FCSTD DOCUMENT  (FreeCAD 1.0R39285 (Git))
Label: CNC-MILL-1
License: All rights reserved
LicenseURL: http://en.wikipedia.org/wiki/All_rights_reserved
objects: Part::Feature×28, Sketcher::SketchObject×24, PartDesign::Pad×18, PartDesign::Body×17, App::Part×15, Part::FeaturePython×14, PartDesign::Pocket×6, PartDesign::Hole×1, PartDesign::Chamfer×1, App::FeaturePython×1
note: 185 computed .brp shape members not serialized (recipe doc carries the construction recipe); baked Part::Feature solids carry a one-line shape summary decoded from their .brp

FEATURE [Part::Feature] Part__Feature  label="NEMA23 - PSM57HS2A54-2P"
  Placement = pos=(161.359,-628.852,-80) rot=(0,0,1;0rad)
  shape: bbox 56.89 x 76.8 x 56.89 mm, 146 faces, 2 solids (baked)
FEATURE [Part::Feature] Part__Feature001  label="NEMA23 - PSM57HS2A54-2P001"
  Placement = pos=(161.359,-628.852,0) rot=(0,0,1;0rad)
  shape: bbox 56.89 x 76.8 x 56.89 mm, 146 faces, 2 solids (baked)
FEATURE [Part::Feature] Part__Feature002  label="NEMA23 - PSM57HS2A54-2P002"
  Placement = pos=(379,33,35) rot=(0,0,1;3.14159rad)
  shape: bbox 56.89 x 76.8 x 56.89 mm, 146 faces, 2 solids (baked)
FEATURE [Sketcher::SketchObject] Sketch
  ArcFitTolerance = 1e-06
  AttachmentSupport = -> [XY_Plane002]
  FullyConstrained = true
  MakeInternals = false
  MapMode = 5
  sketch-geometry (4):
    g0: LineSegment StartX=0 StartY=0 StartZ=0 EndX=257 EndY=0 EndZ=0
    g1: LineSegment StartX=257 StartY=0 StartZ=0 EndX=257 EndY=264 EndZ=0
    g2: LineSegment StartX=257 StartY=264 StartZ=0 EndX=0 EndY=264 EndZ=0
    g3: LineSegment StartX=0 StartY=264 StartZ=0 EndX=0 EndY=0 EndZ=0
  constraints (11):
    c: Coincident(g0,g1)
    c: Coincident(g1,g2)
    c: Coincident(g2,g3)
    c: Coincident(g3,g0)
    c: Horizontal(g0)
    c: Horizontal(g2)
    c: Vertical(g1)
    c: Vertical(g3)
    c: Distance(g1,g3) = 257
    c: Distance(g0,g2) = 264
    c: Coincident(g0,g-1)
FEATURE [PartDesign::Pad] Pad
  Direction = (0,0,1)
  Length = 10
  Length2 = 10
  Profile = -> Sketch
  ReferenceAxis = -> Sketch [N_Axis]
  Suppressed = false
  Type = 0
FEATURE [PartDesign::Body] Body
  AllowCompound = false
  Group = -> [Sketch,Pad]
  Origin = -> Origin002
  Placement = pos=(0,0,-51) rot=(0,0,1;0rad)
  Tip = -> Pad
FEATURE [App::Part] Part001  label="stone table"
  Group = -> [Body]
  Origin = -> Origin
  Placement = pos=(59,-361,0) rot=(0,0,1;0rad)
FEATURE [Sketcher::SketchObject] Sketch001
  ArcFitTolerance = 1e-06
  AttachmentSupport = -> [XZ_Plane004]
  FullyConstrained = true
  MakeInternals = false
  MapMode = 5
  Placement = pos=(0,0,0) rot=(1,0,0;1.5708rad)
  sketch-geometry (14):
    g0: LineSegment StartX=0 StartY=-2 StartZ=0 EndX=0 EndY=-38 EndZ=0
    g1: LineSegment StartX=2 StartY=-40 StartZ=0 EndX=38 EndY=-40 EndZ=0
    g2: LineSegment StartX=40 StartY=-38 StartZ=0 EndX=40 EndY=-2 EndZ=0
    g3: LineSegment StartX=38 StartY=0 StartZ=0 EndX=2 EndY=0 EndZ=0
    g4: ArcOfCircle CenterX=2 CenterY=-2 CenterZ=0 NormalX=0 NormalY=0 NormalZ=1 AngleXU=0 Radius=2 StartAngle=1.5708 EndAngle=3.14159
    g5: ArcOfCircle CenterX=2 CenterY=-38 CenterZ=0 NormalX=0 NormalY=0 NormalZ=1 AngleXU=0 Radius=2 StartAngle=3.14159 EndAngle=4.71239
    g6: ArcOfCircle CenterX=38 CenterY=-38 CenterZ=0 NormalX=0 NormalY=0 NormalZ=1 AngleXU=0 Radius=2 StartAngle=4.71239 EndAngle=6.28319
    g7: ArcOfCircle CenterX=38 CenterY=-2 CenterZ=0 NormalX=0 NormalY=0 NormalZ=1 AngleXU=0 Radius=2 StartAngle=0 EndAngle=1.5708
    g8: LineSegment StartX=2 StartY=-2 StartZ=0 EndX=2 EndY=-38 EndZ=0
    g9: LineSegment StartX=2 StartY=-38 StartZ=0 EndX=38 EndY=-38 EndZ=0
    g10: LineSegment StartX=38 StartY=-38 StartZ=0 EndX=38 EndY=-2 EndZ=0
    g11: LineSegment StartX=38 StartY=-2 StartZ=0 EndX=2 EndY=-2 EndZ=0
    g12: GeomPoint [constr] X=0 Y=0 Z=0
    g13: GeomPoint [constr] X=40 Y=-40 Z=0
  constraints (31):
    c: Tangent(g0,g4) = -1.5708
    c: Tangent(g0,g5) = -1.5708
    c: Tangent(g1,g5) = -1.5708
    c: Tangent(g1,g6) = -1.5708
    c: Tangent(g2,g6) = -1.5708
    c: Tangent(g2,g7) = -1.5708
    c: Tangent(g3,g7) = -1.5708
    c: Tangent(g3,g4) = -1.5708
    c: Vertical(g0)
    c: Vertical(g2)
    c: Horizontal(g1)
    c: Horizontal(g3)
    c: Equal(g4,g5)
    c: Equal(g5,g6)
    c: Equal(g6,g7)
    c: Coincident(g8,g9)
    c: Coincident(g9,g10)
    c: Coincident(g10,g11)
    c: Coincident(g11,g8)
    c: Coincident(g8,g4)
    c: Coincident(g9,g5)
    c: Coincident(g10,g6)
    c: Coincident(g11,g7)
    c: PointOnObject(g12,g0)
    c: PointOnObject(g12,g3)
    c: PointOnObject(g13,g1)
    c: PointOnObject(g13,g2)
    c: Distance(g0,g2) = 40
    c: Distance(g1,g3) = 40
    c: Radius(g5) = 2
    c: Coincident(g12,g-1)
FEATURE [PartDesign::Pad] Pad001
  Direction = (0,-1,2e-16)
  Length = 400
  Length2 = 10
  Placement = pos=(0,0,0) rot=(1,0,0;1.5708rad)
  Profile = -> Sketch001
  ReferenceAxis = -> Sketch001 [N_Axis]
  Suppressed = false
  Type = 0
FEATURE [PartDesign::Body] Body001
  AllowCompound = false
  Group = -> [Sketch001,Pad001]
  Origin = -> Origin004
  Placement = pos=(-54,0,0) rot=(0,0,1;0rad)
  Tip = -> Pad001
FEATURE [Sketcher::SketchObject] Sketch002
  ArcFitTolerance = 1e-06
  AttachmentSupport = -> [XZ_Plane005]
  FullyConstrained = true
  MakeInternals = false
  MapMode = 5
  Placement = pos=(0,0,0) rot=(1,0,0;1.5708rad)
  sketch-geometry (14):
    g0: LineSegment StartX=0 StartY=-2 StartZ=0 EndX=0 EndY=-38 EndZ=0
    g1: LineSegment StartX=2 StartY=-40 StartZ=0 EndX=38 EndY=-40 EndZ=0
    g2: LineSegment StartX=40 StartY=-38 StartZ=0 EndX=40 EndY=-2 EndZ=0
    g3: LineSegment StartX=38 StartY=0 StartZ=0 EndX=2 EndY=0 EndZ=0
    g4: ArcOfCircle CenterX=2 CenterY=-2 CenterZ=0 NormalX=0 NormalY=0 NormalZ=1 AngleXU=0 Radius=2 StartAngle=1.5708 EndAngle=3.14159
    g5: ArcOfCircle CenterX=2 CenterY=-38 CenterZ=0 NormalX=0 NormalY=0 NormalZ=1 AngleXU=0 Radius=2 StartAngle=3.14159 EndAngle=4.71239
    g6: ArcOfCircle CenterX=38 CenterY=-38 CenterZ=0 NormalX=0 NormalY=0 NormalZ=1 AngleXU=0 Radius=2 StartAngle=4.71239 EndAngle=6.28319
    g7: ArcOfCircle CenterX=38 CenterY=-2 CenterZ=0 NormalX=0 NormalY=0 NormalZ=1 AngleXU=0 Radius=2 StartAngle=0 EndAngle=1.5708
    g8: LineSegment StartX=2 StartY=-2 StartZ=0 EndX=2 EndY=-38 EndZ=0
    g9: LineSegment StartX=2 StartY=-38 StartZ=0 EndX=38 EndY=-38 EndZ=0
    g10: LineSegment StartX=38 StartY=-38 StartZ=0 EndX=38 EndY=-2 EndZ=0
    g11: LineSegment StartX=38 StartY=-2 StartZ=0 EndX=2 EndY=-2 EndZ=0
    g12: GeomPoint [constr] X=0 Y=0 Z=0
    g13: GeomPoint [constr] X=40 Y=-40 Z=0
  constraints (31):
    c: Tangent(g0,g4) = -1.5708
    c: Tangent(g0,g5) = -1.5708
    c: Tangent(g1,g5) = -1.5708
    c: Tangent(g1,g6) = -1.5708
    c: Tangent(g2,g6) = -1.5708
    c: Tangent(g2,g7) = -1.5708
    c: Tangent(g3,g7) = -1.5708
    c: Tangent(g3,g4) = -1.5708
    c: Vertical(g0)
    c: Vertical(g2)
    c: Horizontal(g1)
    c: Horizontal(g3)
    c: Equal(g4,g5)
    c: Equal(g5,g6)
    c: Equal(g6,g7)
    c: Coincident(g8,g9)
    c: Coincident(g9,g10)
    c: Coincident(g10,g11)
    c: Coincident(g11,g8)
    c: Coincident(g8,g4)
    c: Coincident(g9,g5)
    c: Coincident(g10,g6)
    c: Coincident(g11,g7)
    c: PointOnObject(g12,g0)
    c: PointOnObject(g12,g3)
    c: PointOnObject(g13,g1)
    c: PointOnObject(g13,g2)
    c: Distance(g0,g2) = 40
    c: Distance(g1,g3) = 40
    c: Radius(g5) = 2
    c: Coincident(g12,g-1)
FEATURE [PartDesign::Pad] Pad002
  Direction = (0,-1,2e-16)
  Length = 400
  Length2 = 10
  Placement = pos=(0,0,0) rot=(1,0,0;1.5708rad)
  Profile = -> Sketch002
  ReferenceAxis = -> Sketch002 [N_Axis]
  Suppressed = false
  Type = 0
FEATURE [PartDesign::Body] Body002
  AllowCompound = false
  Group = -> [Sketch002,Pad002]
  Origin = -> Origin005
  Placement = pos=(346,0,0) rot=(0,0,1;0rad)
  Tip = -> Pad002
FEATURE [Sketcher::SketchObject] Sketch004
  ArcFitTolerance = 1e-06
  AttachmentSupport = -> [XZ_Plane007]
  FullyConstrained = true
  MakeInternals = false
  MapMode = 5
  Placement = pos=(0,0,0) rot=(1,0,0;1.5708rad)
  sketch-geometry (14):
    g0: LineSegment StartX=0 StartY=-2 StartZ=0 EndX=0 EndY=-38 EndZ=0
    g1: LineSegment StartX=2 StartY=-40 StartZ=0 EndX=38 EndY=-40 EndZ=0
    g2: LineSegment StartX=40 StartY=-38 StartZ=0 EndX=40 EndY=-2 EndZ=0
    g3: LineSegment StartX=38 StartY=0 StartZ=0 EndX=2 EndY=0 EndZ=0
    g4: ArcOfCircle CenterX=2 CenterY=-2 CenterZ=0 NormalX=0 NormalY=0 NormalZ=1 AngleXU=0 Radius=2 StartAngle=1.5708 EndAngle=3.14159
    g5: ArcOfCircle CenterX=2 CenterY=-38 CenterZ=0 NormalX=0 NormalY=0 NormalZ=1 AngleXU=0 Radius=2 StartAngle=3.14159 EndAngle=4.71239
    g6: ArcOfCircle CenterX=38 CenterY=-38 CenterZ=0 NormalX=0 NormalY=0 NormalZ=1 AngleXU=0 Radius=2 StartAngle=4.71239 EndAngle=6.28319
    g7: ArcOfCircle CenterX=38 CenterY=-2 CenterZ=0 NormalX=0 NormalY=0 NormalZ=1 AngleXU=0 Radius=2 StartAngle=0 EndAngle=1.5708
    g8: LineSegment StartX=2 StartY=-2 StartZ=0 EndX=2 EndY=-38 EndZ=0
    g9: LineSegment StartX=2 StartY=-38 StartZ=0 EndX=38 EndY=-38 EndZ=0
    g10: LineSegment StartX=38 StartY=-38 StartZ=0 EndX=38 EndY=-2 EndZ=0
    g11: LineSegment StartX=38 StartY=-2 StartZ=0 EndX=2 EndY=-2 EndZ=0
    g12: GeomPoint [constr] X=0 Y=0 Z=0
    g13: GeomPoint [constr] X=40 Y=-40 Z=0
  constraints (31):
    c: Tangent(g0,g4) = -1.5708
    c: Tangent(g0,g5) = -1.5708
    c: Tangent(g1,g5) = -1.5708
    c: Tangent(g1,g6) = -1.5708
    c: Tangent(g2,g6) = -1.5708
    c: Tangent(g2,g7) = -1.5708
    c: Tangent(g3,g7) = -1.5708
    c: Tangent(g3,g4) = -1.5708
    c: Vertical(g0)
    c: Vertical(g2)
    c: Horizontal(g1)
    c: Horizontal(g3)
    c: Equal(g4,g5)
    c: Equal(g5,g6)
    c: Equal(g6,g7)
    c: Coincident(g8,g9)
    c: Coincident(g9,g10)
    c: Coincident(g10,g11)
    c: Coincident(g11,g8)
    c: Coincident(g8,g4)
    c: Coincident(g9,g5)
    c: Coincident(g10,g6)
    c: Coincident(g11,g7)
    c: PointOnObject(g12,g0)
    c: PointOnObject(g12,g3)
    c: PointOnObject(g13,g1)
    c: PointOnObject(g13,g2)
    c: Distance(g0,g2) = 40
    c: Distance(g1,g3) = 40
    c: Radius(g5) = 2
    c: Coincident(g12,g-1)
FEATURE [PartDesign::Pad] Pad004
  Direction = (0,-1,2e-16)
  Length = 400
  Length2 = 10
  Placement = pos=(0,0,0) rot=(1,0,0;1.5708rad)
  Profile = -> Sketch004
  ReferenceAxis = -> Sketch004 [N_Axis]
  Suppressed = false
  Type = 0
FEATURE [Sketcher::SketchObject] Sketch005
  ArcFitTolerance = 1e-06
  AttachmentSupport = -> [XY_Plane009]
  FullyConstrained = true
  MakeInternals = false
  MapMode = 5
  sketch-geometry (16):
    g0: LineSegment StartX=0 StartY=68 StartZ=0 EndX=65 EndY=68 EndZ=0
    g1: LineSegment StartX=65 StartY=68 StartZ=0 EndX=65 EndY=6.00001 EndZ=0
    g2: LineSegment StartX=65 StartY=6.00001 StartZ=0 EndX=59 EndY=0 EndZ=0
    g3: LineSegment StartX=0 StartY=68 StartZ=0 EndX=0 EndY=6.00001 EndZ=0
    g4: LineSegment StartX=0 StartY=6.00001 StartZ=0 EndX=6 EndY=0 EndZ=0
    g5: LineSegment StartX=6 StartY=0 StartZ=0 EndX=59 EndY=0 EndZ=0
    g6: ArcOfCircle CenterX=52.5 CenterY=10 CenterZ=0 NormalX=0 NormalY=0 NormalZ=1 AngleXU=0 Radius=2 StartAngle=3.14159 EndAngle=6.28319
    g7: ArcOfCircle CenterX=52.5 CenterY=52 CenterZ=0 NormalX=0 NormalY=0 NormalZ=1 AngleXU=0 Radius=2 StartAngle=0 EndAngle=3.14159
    g8: LineSegment StartX=50.5 StartY=10 StartZ=0 EndX=50.5 EndY=52 EndZ=0
    g9: LineSegment StartX=54.5 StartY=10 StartZ=0 EndX=54.5 EndY=52 EndZ=0
    g10: ArcOfCircle CenterX=12.5 CenterY=10 CenterZ=0 NormalX=0 NormalY=0 NormalZ=1 AngleXU=0 Radius=2 StartAngle=3.14159 EndAngle=6.28319
    g11: ArcOfCircle CenterX=12.5 CenterY=52 CenterZ=0 NormalX=0 NormalY=0 NormalZ=1 AngleXU=0 Radius=2 StartAngle=0 EndAngle=3.14159
    g12: LineSegment StartX=14.5 StartY=10 StartZ=0 EndX=14.5 EndY=52 EndZ=0
    g13: LineSegment StartX=10.5 StartY=10 StartZ=0 EndX=10.5 EndY=52 EndZ=0
    g14: LineSegment [constr] StartX=32.5 StartY=68 StartZ=0 EndX=32.5 EndY=0 EndZ=0
    g15: LineSegment [constr] StartX=65 StartY=31 StartZ=0 EndX=0 EndY=31 EndZ=0
  constraints (46):
    c: PointOnObject(g0,g-2)
    c: Distance(g0) = 65
    c: Horizontal(g0)
    c: Distance(g1) = 62
    c: Coincident(g1,g0)
    c: Vertical(g1)
    c: Angle(g-1,g2) = -2.35619
    c: Coincident(g2,g1)
    c: PointOnObject(g2,g-1)
    c: Distance(g3) = 62
    c: Vertical(g3)
    c: Coincident(g4,g3)
    c: Coincident(g5,g4)
    c: Coincident(g5,g2)
    c: Horizontal(g5)
    c: Tangent(g6,g8) = 1.5708
    c: Tangent(g6,g9) = -1.5708
    c: Tangent(g7,g8) = 1.5708
    c: Tangent(g7,g9) = -1.5708
    c: Equal(g6,g7)
    c: Vertical(g9)
    c: Distance(g6,g7) = 42
    c: Radius(g6) = 2
    c: Tangent(g10,g12) = -1.5708
    c: Tangent(g10,g13) = 1.5708
    c: Tangent(g11,g12) = -1.5708
    c: Tangent(g11,g13) = 1.5708
    c: Equal(g10,g11)
    c: Vertical(g13)
    c: Distance(g10,g11) = 42
    c: Radius(g10) = 2
    c: Distance(g-1,g4) = 6
    c: DistanceX(g4,g2) = 53
    c: DistanceX(g10,g6) = 40
    c: Symmetric(g0,g0,g14)
    c: Vertical(g14)
    c: DistanceX(g10,g14) = 20
    c: DistanceX(g3,g1) = 65
    c: PointOnObject(g15,g1)
    c: PointOnObject(g15,g3)
    c: Horizontal(g15)
    c: DistanceY(g-1,g15) = 31
    c: DistanceY(g10,g15) = 21
    c: Horizontal(g10,g6)
    c: Horizontal(g3,g1)
    c: Horizontal(g4,g14)
FEATURE [PartDesign::Pad] Pad005
  Direction = (0,0,1)
  Length = 3
  Length2 = 10
  Profile = -> Sketch005
  ReferenceAxis = -> Sketch005 [N_Axis]
  Suppressed = false
  Type = 0
FEATURE [Part::Feature] Part__Feature003  label="MGN9-H"
  shape: bbox 20 x 8 x 29.9 mm, 47 faces (baked)
FEATURE [Part::Feature] Part__Feature004  label="MGN9-H001"
  shape: bbox 20 x 7.7 x 4.1 mm, 23 faces (baked)
FEATURE [Part::Feature] Part__Feature005  label="MGN9-H002"
  shape: bbox 2.603 x 2.603 x 1.283 mm, 15 faces (baked)
FEATURE [Part::Feature] Part__Feature006  label="MGN9-H003"
  shape: bbox 2.603 x 2.603 x 1.283 mm, 15 faces (baked)
FEATURE [Part::Feature] Part__Feature007  label="MGN9-H004"
  shape: bbox 20 x 7.7 x 0.9 mm, 57 faces (baked)
FEATURE [Part::Feature] Part__Feature008  label="MGN9-H005"
  shape: bbox 20 x 7.7 x 4.1 mm, 23 faces (baked)
FEATURE [Part::Feature] Part__Feature009  label="MGN9-H006"
  shape: bbox 20 x 7.7 x 0.9 mm, 57 faces (baked)
FEATURE [Part::Feature] Part__Feature010  label="MGN9-H007"
  shape: bbox 2.603 x 2.603 x 1.283 mm, 15 faces (baked)
FEATURE [Part::Feature] Part__Feature011  label="MGN9-H008"
  shape: bbox 2.603 x 2.603 x 1.283 mm, 15 faces (baked)
FEATURE [App::Part] MGN9_H  label="MGN9-H009 block"
  Group = -> [Part__Feature003,Part__Feature004,Part__Feature005,Part__Feature006,Part__Feature007,Part__Feature008,Part__Feature009,Part__Feature010,Part__Feature011]
  Origin = -> Origin010
  Placement = pos=(19,-161.179,6) rot=(0,0.707107,0.707107;3.14159rad)
FEATURE [Part::Feature] Part__Feature012  label="MGN9"
  Placement = pos=(-3.25,-34,143.25) rot=(0,0,1;1.5708rad)
  shape: bbox 6.5 x 9 x 250 mm, 130 faces (baked)
FEATURE [App::Part] Part004  label="MGN9 rail"
  Group = -> [Part__Feature012]
  Origin = -> Origin011
  Placement = pos=(53,8.58707,0) rot=(-0.58,-0.58,0.58;4.18879rad)
FEATURE [Sketcher::SketchObject] Sketch006
  ArcFitTolerance = 1e-06
  AttachmentSupport = -> [Pad005]
  FullyConstrained = true
  MakeInternals = false
  MapMode = 5
  Placement = pos=(0,0,3) rot=(0,0,1;0rad)
  sketch-geometry (4):
    g0: LineSegment StartX=0 StartY=68 StartZ=0 EndX=0 EndY=65 EndZ=0
    g1: LineSegment StartX=0 StartY=65 StartZ=0 EndX=65 EndY=65 EndZ=0
    g2: LineSegment StartX=65 StartY=65 StartZ=0 EndX=65 EndY=68 EndZ=0
    g3: LineSegment StartX=65 StartY=68 StartZ=0 EndX=0 EndY=68 EndZ=0
  constraints (12):
    c: Coincident(g0,g1)
    c: Coincident(g1,g2)
    c: Coincident(g2,g3)
    c: Coincident(g3,g0)
    c: Vertical(g0)
    c: Vertical(g2)
    c: Horizontal(g1)
    c: Horizontal(g3)
    c: Distance(g0,g2) = 65
    c: Distance(g1,g3) = 3
    c: PointOnObject(g0,g-2)
    c: DistanceY(g-1,g0) = 68
FEATURE [PartDesign::Pad] Pad006
  BaseFeature = -> Pad005
  Direction = (0,0,1)
  Length = 65
  Length2 = 10
  Profile = -> Sketch006
  ReferenceAxis = -> Sketch006 [N_Axis]
  Suppressed = false
  Type = 0
FEATURE [Sketcher::SketchObject] Sketch007
  ArcFitTolerance = 1e-06
  AttachmentSupport = -> [Pad006]
  ExternalGeometry = -> [Pad006]
  FullyConstrained = false
  MakeInternals = false
  MapMode = 5
  Placement = pos=(0,65,0) rot=(1,0,0;1.5708rad)
  sketch-geometry (15):
    g0: LineSegment StartX=0 StartY=68 StartZ=0 EndX=6 EndY=68 EndZ=0
    g1: LineSegment StartX=0 StartY=68 StartZ=0 EndX=0 EndY=62 EndZ=0
    g2: LineSegment StartX=6 StartY=68 StartZ=0 EndX=0 EndY=62 EndZ=0
    g3: LineSegment [constr] StartX=32.5 StartY=68 StartZ=0 EndX=32.5 EndY=3 EndZ=0
    g4: Circle CenterX=9 CenterY=59 CenterZ=0 NormalX=0 NormalY=0 NormalZ=1 AngleXU=0 Radius=2.6
    g5: LineSegment [constr] StartX=0 StartY=35.5 StartZ=0 EndX=65 EndY=35.5 EndZ=0
    g6: Circle CenterX=32.5 CenterY=35.5 CenterZ=0 NormalX=0 NormalY=0 NormalZ=1 AngleXU=0 Radius=19.1
    g7: LineSegment StartX=65 StartY=68 StartZ=0 EndX=59 EndY=68 EndZ=0
    g8: LineSegment StartX=65 StartY=68 StartZ=0 EndX=65 EndY=62 EndZ=0
    g9: LineSegment StartX=59 StartY=68 StartZ=0 EndX=65 EndY=62 EndZ=0
    g10: Circle CenterX=56 CenterY=12 CenterZ=0 NormalX=0 NormalY=0 NormalZ=1 AngleXU=0 Radius=2.6
    g11: Circle CenterX=56 CenterY=59 CenterZ=0 NormalX=0 NormalY=0 NormalZ=1 AngleXU=0 Radius=2.6
    g12: Circle CenterX=56 CenterY=12 CenterZ=0 NormalX=0 NormalY=0 NormalZ=1 AngleXU=0 Radius=2.6
    g13: Circle CenterX=9 CenterY=12 CenterZ=0 NormalX=0 NormalY=0 NormalZ=1 AngleXU=0 Radius=2.6
    g14: Circle CenterX=9 CenterY=12 CenterZ=0 NormalX=0 NormalY=0 NormalZ=1 AngleXU=0 Radius=2.6
  constraints (32):
    c: Distance(g0) = 6
    c: PointOnObject(g0,g-2)
    c: Horizontal(g0)
    c: Distance(g1) = 6
    c: Coincident(g1,g0)
    c: PointOnObject(g1,g-2)
    c: Coincident(g2,g0)
    c: Coincident(g2,g1)
    c: Vertical(g3)
    c: DistanceX(g4,g3) = 23.5
    c: Distance(g5) = 65
    c: Symmetric(g-3,g-3,g5)
    c: Horizontal(g5)
    c: Diameter(g6) = 38.2
    c: Symmetric(g5,g5,g6)
    c: DistanceY(g-3,g0) = 65
    c: Distance(g7) = 6
    c: Horizontal(g7)
    c: Distance(g8) = 6
    c: Coincident(g8,g7)
    c: Coincident(g9,g7)
    c: Coincident(g9,g8)
    c: Diameter(g12) = 5.2
    c: Coincident(g12,g10)
    c: Horizontal(g3,g0)
    c: Symmetric(g4,g11,g3)
    c: Diameter(g14) = 5.2
    c: Coincident(g14,g13)
    c: Symmetric(g13,g10,g3)
    c: Horizontal(g3,g-3)
    c: Vertical(g5,g8)
    c: DistanceX(g0,g3) = 32.5
FEATURE [PartDesign::Pocket] Pocket
  BaseFeature = -> Pad006
  Direction = (0,1,-2e-16)
  Length = 3
  Length2 = 5
  Profile = -> Sketch007
  ReferenceAxis = -> Sketch007 [N_Axis]
  Suppressed = false
  Type = 0
FEATURE [PartDesign::Body] Body005
  AllowCompound = false
  Group = -> [Sketch005,Pad005,Sketch006,Pad006,Sketch007,Pocket]
  Origin = -> Origin009
  Placement = pos=(12,0,0) rot=(0,0,1;0rad)
  Tip = -> Pocket
FEATURE [App::Part] Part003  label="bracket nema 23"
  Group = -> [Body005]
  Origin = -> Origin008
  Placement = pos=(63,70,0) rot=(0,0,1;3.14159rad)
FEATURE [App::Part] Part005  label="TR8x2 screw"
  Origin = -> Origin012
FEATURE [Part::FeaturePython] ThreadedRod  label="8x400-ThreadedRod"  # WARN: FeaturePython — macro-defined, semantics opaque (R4)
  Diameter = 29
  DiameterCustom = 8
  Invert = false
  LeftHanded = false
  Length = 400
  MatchOuter = false
  OffsetAngle = 0
  PitchCustom = 2
  Placement = pos=(19,-418,35) rot=(1,0,0;1.5708rad)
  Thread = false
  Type = 4
FEATURE [Part::Feature] Part__Feature013  label="Coupler 6.35-8mm Without Screw"
  shape: bbox 20.93 x 20.57 x 29.69 mm, 170 faces (baked)
FEATURE [Part::Feature] Part__Feature014  label="80 x 60 x 32 - EG 86-32 HG (All closed) [similar]"
  Placement = pos=(169,-174.833,-46.8462) rot=(-1,0,0;4.71239rad)
  shape: bbox 800 x 600 x 320 mm, 837 faces (baked)
FEATURE [Part::Feature] Part__Feature015  label="60 x 40 x 27 - EG 64-27 HG (All closed) [similar]"
  Placement = pos=(186,-256,-359) rot=(-0.57735,0.57735,0.57735;4.18879rad)
  shape: bbox 398 x 598 x 270 mm, 709 faces (baked)
FEATURE [App::Part] Part006  label="Bottom container"
  Group = -> [Part__Feature014,Part__Feature015]
  Origin = -> Origin015
FEATURE [Sketcher::SketchObject] Sketch008
  ArcFitTolerance = 1e-06
  AttachmentSupport = -> [XZ_Plane017]
  FullyConstrained = true
  MakeInternals = false
  MapMode = 5
  Placement = pos=(0,0,0) rot=(1,0,0;1.5708rad)
  sketch-geometry (14):
    g0: LineSegment StartX=0 StartY=-2 StartZ=0 EndX=0 EndY=-38 EndZ=0
    g1: LineSegment StartX=2 StartY=-40 StartZ=0 EndX=38 EndY=-40 EndZ=0
    g2: LineSegment StartX=40 StartY=-38 StartZ=0 EndX=40 EndY=-2 EndZ=0
    g3: LineSegment StartX=38 StartY=0 StartZ=0 EndX=2 EndY=0 EndZ=0
    g4: ArcOfCircle CenterX=2 CenterY=-2 CenterZ=0 NormalX=0 NormalY=0 NormalZ=1 AngleXU=0 Radius=2 StartAngle=1.5708 EndAngle=3.14159
    g5: ArcOfCircle CenterX=2 CenterY=-38 CenterZ=0 NormalX=0 NormalY=0 NormalZ=1 AngleXU=0 Radius=2 StartAngle=3.14159 EndAngle=4.71239
    g6: ArcOfCircle CenterX=38 CenterY=-38 CenterZ=0 NormalX=0 NormalY=0 NormalZ=1 AngleXU=0 Radius=2 StartAngle=4.71239 EndAngle=6.28319
    g7: ArcOfCircle CenterX=38 CenterY=-2 CenterZ=0 NormalX=0 NormalY=0 NormalZ=1 AngleXU=0 Radius=2 StartAngle=0 EndAngle=1.5708
    g8: LineSegment StartX=2 StartY=-2 StartZ=0 EndX=2 EndY=-38 EndZ=0
    g9: LineSegment StartX=2 StartY=-38 StartZ=0 EndX=38 EndY=-38 EndZ=0
    g10: LineSegment StartX=38 StartY=-38 StartZ=0 EndX=38 EndY=-2 EndZ=0
    g11: LineSegment StartX=38 StartY=-2 StartZ=0 EndX=2 EndY=-2 EndZ=0
    g12: GeomPoint [constr] X=0 Y=0 Z=0
    g13: GeomPoint [constr] X=40 Y=-40 Z=0
  constraints (31):
    c: Tangent(g0,g4) = -1.5708
    c: Tangent(g0,g5) = -1.5708
    c: Tangent(g1,g5) = -1.5708
    c: Tangent(g1,g6) = -1.5708
    c: Tangent(g2,g6) = -1.5708
    c: Tangent(g2,g7) = -1.5708
    c: Tangent(g3,g7) = -1.5708
    c: Tangent(g3,g4) = -1.5708
    c: Vertical(g0)
    c: Vertical(g2)
    c: Horizontal(g1)
    c: Horizontal(g3)
    c: Equal(g4,g5)
    c: Equal(g5,g6)
    c: Equal(g6,g7)
    c: Coincident(g8,g9)
    c: Coincident(g9,g10)
    c: Coincident(g10,g11)
    c: Coincident(g11,g8)
    c: Coincident(g8,g4)
    c: Coincident(g9,g5)
    c: Coincident(g10,g6)
    c: Coincident(g11,g7)
    c: PointOnObject(g12,g0)
    c: PointOnObject(g12,g3)
    c: PointOnObject(g13,g1)
    c: PointOnObject(g13,g2)
    c: Distance(g0,g2) = 40
    c: Distance(g1,g3) = 40
    c: Radius(g5) = 2
    c: Coincident(g12,g-1)
FEATURE [PartDesign::Pad] Pad007
  Direction = (0,-1,2e-16)
  Length = 400
  Length2 = 10
  Placement = pos=(0,0,0) rot=(1,0,0;1.5708rad)
  Profile = -> Sketch008
  ReferenceAxis = -> Sketch008 [N_Axis]
  Suppressed = false
  Type = 0
FEATURE [PartDesign::Body] Body006
  AllowCompound = false
  Group = -> [Sketch008,Pad007]
  Origin = -> Origin017
  Placement = pos=(386,40,0) rot=(-0.57735,0.57735,0.57735;4.18879rad)
  Tip = -> Pad007
FEATURE [Sketcher::SketchObject] Sketch009
  ArcFitTolerance = 1e-06
  AttachmentSupport = -> [XZ_Plane018]
  FullyConstrained = true
  MakeInternals = false
  MapMode = 5
  Placement = pos=(0,0,0) rot=(1,0,0;1.5708rad)
  sketch-geometry (14):
    g0: LineSegment StartX=0 StartY=-2 StartZ=0 EndX=0 EndY=-38 EndZ=0
    g1: LineSegment StartX=2 StartY=-40 StartZ=0 EndX=38 EndY=-40 EndZ=0
    g2: LineSegment StartX=40 StartY=-38 StartZ=0 EndX=40 EndY=-2 EndZ=0
    g3: LineSegment StartX=38 StartY=0 StartZ=0 EndX=2 EndY=0 EndZ=0
    g4: ArcOfCircle CenterX=2 CenterY=-2 CenterZ=0 NormalX=0 NormalY=0 NormalZ=1 AngleXU=0 Radius=2 StartAngle=1.5708 EndAngle=3.14159
    g5: ArcOfCircle CenterX=2 CenterY=-38 CenterZ=0 NormalX=0 NormalY=0 NormalZ=1 AngleXU=0 Radius=2 StartAngle=3.14159 EndAngle=4.71239
    g6: ArcOfCircle CenterX=38 CenterY=-38 CenterZ=0 NormalX=0 NormalY=0 NormalZ=1 AngleXU=0 Radius=2 StartAngle=4.71239 EndAngle=6.28319
    g7: ArcOfCircle CenterX=38 CenterY=-2 CenterZ=0 NormalX=0 NormalY=0 NormalZ=1 AngleXU=0 Radius=2 StartAngle=0 EndAngle=1.5708
    g8: LineSegment StartX=2 StartY=-2 StartZ=0 EndX=2 EndY=-38 EndZ=0
    g9: LineSegment StartX=2 StartY=-38 StartZ=0 EndX=38 EndY=-38 EndZ=0
    g10: LineSegment StartX=38 StartY=-38 StartZ=0 EndX=38 EndY=-2 EndZ=0
    g11: LineSegment StartX=38 StartY=-2 StartZ=0 EndX=2 EndY=-2 EndZ=0
    g12: GeomPoint [constr] X=0 Y=0 Z=0
    g13: GeomPoint [constr] X=40 Y=-40 Z=0
  constraints (31):
    c: Tangent(g0,g4) = -1.5708
    c: Tangent(g0,g5) = -1.5708
    c: Tangent(g1,g5) = -1.5708
    c: Tangent(g1,g6) = -1.5708
    c: Tangent(g2,g6) = -1.5708
    c: Tangent(g2,g7) = -1.5708
    c: Tangent(g3,g7) = -1.5708
    c: Tangent(g3,g4) = -1.5708
    c: Vertical(g0)
    c: Vertical(g2)
    c: Horizontal(g1)
    c: Horizontal(g3)
    c: Equal(g4,g5)
    c: Equal(g5,g6)
    c: Equal(g6,g7)
    c: Coincident(g8,g9)
    c: Coincident(g9,g10)
    c: Coincident(g10,g11)
    c: Coincident(g11,g8)
    c: Coincident(g8,g4)
    c: Coincident(g9,g5)
    c: Coincident(g10,g6)
    c: Coincident(g11,g7)
    c: PointOnObject(g12,g0)
    c: PointOnObject(g12,g3)
    c: PointOnObject(g13,g1)
    c: PointOnObject(g13,g2)
    c: Distance(g0,g2) = 40
    c: Distance(g1,g3) = 40
    c: Radius(g5) = 2
    c: Coincident(g12,g-1)
FEATURE [PartDesign::Pad] Pad008
  Direction = (0,-1,2e-16)
  Length = 400
  Length2 = 10
  Placement = pos=(0,0,0) rot=(1,0,0;1.5708rad)
  Profile = -> Sketch009
  ReferenceAxis = -> Sketch009 [N_Axis]
  Suppressed = false
  Type = 0
FEATURE [PartDesign::Body] Body007
  AllowCompound = false
  Group = -> [Sketch009,Pad008]
  Origin = -> Origin018
  Placement = pos=(-54,40,9.77e-14) rot=(-0.57735,0.57735,0.57735;4.18879rad)
  Tip = -> Pad008
FEATURE [Sketcher::SketchObject] Sketch010
  ArcFitTolerance = 1e-06
  AttachmentSupport = -> [XZ_Plane019]
  FullyConstrained = true
  MakeInternals = false
  MapMode = 5
  Placement = pos=(0,0,0) rot=(1,0,0;1.5708rad)
  sketch-geometry (14):
    g0: LineSegment StartX=0 StartY=-2 StartZ=0 EndX=0 EndY=-38 EndZ=0
    g1: LineSegment StartX=2 StartY=-40 StartZ=0 EndX=38 EndY=-40 EndZ=0
    g2: LineSegment StartX=40 StartY=-38 StartZ=0 EndX=40 EndY=-2 EndZ=0
    g3: LineSegment StartX=38 StartY=0 StartZ=0 EndX=2 EndY=0 EndZ=0
    g4: ArcOfCircle CenterX=2 CenterY=-2 CenterZ=0 NormalX=0 NormalY=0 NormalZ=1 AngleXU=0 Radius=2 StartAngle=1.5708 EndAngle=3.14159
    g5: ArcOfCircle CenterX=2 CenterY=-38 CenterZ=0 NormalX=0 NormalY=0 NormalZ=1 AngleXU=0 Radius=2 StartAngle=3.14159 EndAngle=4.71239
    g6: ArcOfCircle CenterX=38 CenterY=-38 CenterZ=0 NormalX=0 NormalY=0 NormalZ=1 AngleXU=0 Radius=2 StartAngle=4.71239 EndAngle=6.28319
    g7: ArcOfCircle CenterX=38 CenterY=-2 CenterZ=0 NormalX=0 NormalY=0 NormalZ=1 AngleXU=0 Radius=2 StartAngle=0 EndAngle=1.5708
    g8: LineSegment StartX=2 StartY=-2 StartZ=0 EndX=2 EndY=-38 EndZ=0
    g9: LineSegment StartX=2 StartY=-38 StartZ=0 EndX=38 EndY=-38 EndZ=0
    g10: LineSegment StartX=38 StartY=-38 StartZ=0 EndX=38 EndY=-2 EndZ=0
    g11: LineSegment StartX=38 StartY=-2 StartZ=0 EndX=2 EndY=-2 EndZ=0
    g12: GeomPoint [constr] X=0 Y=0 Z=0
    g13: GeomPoint [constr] X=40 Y=-40 Z=0
  constraints (31):
    c: Tangent(g0,g4) = -1.5708
    c: Tangent(g0,g5) = -1.5708
    c: Tangent(g1,g5) = -1.5708
    c: Tangent(g1,g6) = -1.5708
    c: Tangent(g2,g6) = -1.5708
    c: Tangent(g2,g7) = -1.5708
    c: Tangent(g3,g7) = -1.5708
    c: Tangent(g3,g4) = -1.5708
    c: Vertical(g0)
    c: Vertical(g2)
    c: Horizontal(g1)
    c: Horizontal(g3)
    c: Equal(g4,g5)
    c: Equal(g5,g6)
    c: Equal(g6,g7)
    c: Coincident(g8,g9)
    c: Coincident(g9,g10)
    c: Coincident(g10,g11)
    c: Coincident(g11,g8)
    c: Coincident(g8,g4)
    c: Coincident(g9,g5)
    c: Coincident(g10,g6)
    c: Coincident(g11,g7)
    c: PointOnObject(g12,g0)
    c: PointOnObject(g12,g3)
    c: PointOnObject(g13,g1)
    c: PointOnObject(g13,g2)
    c: Distance(g0,g2) = 40
    c: Distance(g1,g3) = 40
    c: Radius(g5) = 2
    c: Coincident(g12,g-1)
FEATURE [PartDesign::Pad] Pad009
  Direction = (0,-1,2e-16)
  Length = 400
  Length2 = 10
  Placement = pos=(0,0,0) rot=(1,0,0;1.5708rad)
  Profile = -> Sketch010
  ReferenceAxis = -> Sketch010 [N_Axis]
  Suppressed = false
  Type = 0
FEATURE [PartDesign::Body] Body008
  AllowCompound = false
  Group = -> [Sketch010,Pad009]
  Origin = -> Origin019
  Placement = pos=(386,-400,9.77e-14) rot=(-0.57735,0.57735,0.57735;4.18879rad)
  Tip = -> Pad009
FEATURE [Sketcher::SketchObject] Sketch011
  ArcFitTolerance = 1e-06
  AttachmentSupport = -> [XZ_Plane020]
  FullyConstrained = true
  MakeInternals = false
  MapMode = 5
  Placement = pos=(0,0,0) rot=(1,0,0;1.5708rad)
  sketch-geometry (14):
    g0: LineSegment StartX=0 StartY=-2 StartZ=0 EndX=0 EndY=-38 EndZ=0
    g1: LineSegment StartX=2 StartY=-40 StartZ=0 EndX=38 EndY=-40 EndZ=0
    g2: LineSegment StartX=40 StartY=-38 StartZ=0 EndX=40 EndY=-2 EndZ=0
    g3: LineSegment StartX=38 StartY=0 StartZ=0 EndX=2 EndY=0 EndZ=0
    g4: ArcOfCircle CenterX=2 CenterY=-2 CenterZ=0 NormalX=0 NormalY=0 NormalZ=1 AngleXU=0 Radius=2 StartAngle=1.5708 EndAngle=3.14159
    g5: ArcOfCircle CenterX=2 CenterY=-38 CenterZ=0 NormalX=0 NormalY=0 NormalZ=1 AngleXU=0 Radius=2 StartAngle=3.14159 EndAngle=4.71239
    g6: ArcOfCircle CenterX=38 CenterY=-38 CenterZ=0 NormalX=0 NormalY=0 NormalZ=1 AngleXU=0 Radius=2 StartAngle=4.71239 EndAngle=6.28319
    g7: ArcOfCircle CenterX=38 CenterY=-2 CenterZ=0 NormalX=0 NormalY=0 NormalZ=1 AngleXU=0 Radius=2 StartAngle=0 EndAngle=1.5708
    g8: LineSegment StartX=2 StartY=-2 StartZ=0 EndX=2 EndY=-38 EndZ=0
    g9: LineSegment StartX=2 StartY=-38 StartZ=0 EndX=38 EndY=-38 EndZ=0
    g10: LineSegment StartX=38 StartY=-38 StartZ=0 EndX=38 EndY=-2 EndZ=0
    g11: LineSegment StartX=38 StartY=-2 StartZ=0 EndX=2 EndY=-2 EndZ=0
    g12: GeomPoint [constr] X=0 Y=0 Z=0
    g13: GeomPoint [constr] X=40 Y=-40 Z=0
  constraints (31):
    c: Tangent(g0,g4) = -1.5708
    c: Tangent(g0,g5) = -1.5708
    c: Tangent(g1,g5) = -1.5708
    c: Tangent(g1,g6) = -1.5708
    c: Tangent(g2,g6) = -1.5708
    c: Tangent(g2,g7) = -1.5708
    c: Tangent(g3,g7) = -1.5708
    c: Tangent(g3,g4) = -1.5708
    c: Vertical(g0)
    c: Vertical(g2)
    c: Horizontal(g1)
    c: Horizontal(g3)
    c: Equal(g4,g5)
    c: Equal(g5,g6)
    c: Equal(g6,g7)
    c: Coincident(g8,g9)
    c: Coincident(g9,g10)
    c: Coincident(g10,g11)
    c: Coincident(g11,g8)
    c: Coincident(g8,g4)
    c: Coincident(g9,g5)
    c: Coincident(g10,g6)
    c: Coincident(g11,g7)
    c: PointOnObject(g12,g0)
    c: PointOnObject(g12,g3)
    c: PointOnObject(g13,g1)
    c: PointOnObject(g13,g2)
    c: Distance(g0,g2) = 40
    c: Distance(g1,g3) = 40
    c: Radius(g5) = 2
    c: Coincident(g12,g-1)
FEATURE [PartDesign::Pad] Pad010
  Direction = (0,-1,2e-16)
  Length = 400
  Length2 = 10
  Placement = pos=(0,0,0) rot=(1,0,0;1.5708rad)
  Profile = -> Sketch011
  ReferenceAxis = -> Sketch011 [N_Axis]
  Suppressed = false
  Type = 0
FEATURE [PartDesign::Body] Body009
  AllowCompound = false
  Group = -> [Sketch011,Pad010]
  Origin = -> Origin020
  Placement = pos=(-54,-400,1.954e-13) rot=(-0.57735,0.57735,0.57735;4.18879rad)
  Tip = -> Pad010
FEATURE [Sketcher::SketchObject] Sketch012
  ArcFitTolerance = 1e-06
  AttachmentSupport = -> [XZ_Plane021]
  FullyConstrained = true
  MakeInternals = false
  MapMode = 5
  Placement = pos=(0,0,0) rot=(1,0,0;1.5708rad)
  sketch-geometry (14):
    g0: LineSegment StartX=0 StartY=-2 StartZ=0 EndX=0 EndY=-38 EndZ=0
    g1: LineSegment StartX=2 StartY=-40 StartZ=0 EndX=38 EndY=-40 EndZ=0
    g2: LineSegment StartX=40 StartY=-38 StartZ=0 EndX=40 EndY=-2 EndZ=0
    g3: LineSegment StartX=38 StartY=0 StartZ=0 EndX=2 EndY=0 EndZ=0
    g4: ArcOfCircle CenterX=2 CenterY=-2 CenterZ=0 NormalX=0 NormalY=0 NormalZ=1 AngleXU=0 Radius=2 StartAngle=1.5708 EndAngle=3.14159
    g5: ArcOfCircle CenterX=2 CenterY=-38 CenterZ=0 NormalX=0 NormalY=0 NormalZ=1 AngleXU=0 Radius=2 StartAngle=3.14159 EndAngle=4.71239
    g6: ArcOfCircle CenterX=38 CenterY=-38 CenterZ=0 NormalX=0 NormalY=0 NormalZ=1 AngleXU=0 Radius=2 StartAngle=4.71239 EndAngle=6.28319
    g7: ArcOfCircle CenterX=38 CenterY=-2 CenterZ=0 NormalX=0 NormalY=0 NormalZ=1 AngleXU=0 Radius=2 StartAngle=0 EndAngle=1.5708
    g8: LineSegment StartX=2 StartY=-2 StartZ=0 EndX=2 EndY=-38 EndZ=0
    g9: LineSegment StartX=2 StartY=-38 StartZ=0 EndX=38 EndY=-38 EndZ=0
    g10: LineSegment StartX=38 StartY=-38 StartZ=0 EndX=38 EndY=-2 EndZ=0
    g11: LineSegment StartX=38 StartY=-2 StartZ=0 EndX=2 EndY=-2 EndZ=0
    g12: GeomPoint [constr] X=0 Y=0 Z=0
    g13: GeomPoint [constr] X=40 Y=-40 Z=0
  constraints (31):
    c: Tangent(g0,g4) = -1.5708
    c: Tangent(g0,g5) = -1.5708
    c: Tangent(g1,g5) = -1.5708
    c: Tangent(g1,g6) = -1.5708
    c: Tangent(g2,g6) = -1.5708
    c: Tangent(g2,g7) = -1.5708
    c: Tangent(g3,g7) = -1.5708
    c: Tangent(g3,g4) = -1.5708
    c: Vertical(g0)
    c: Vertical(g2)
    c: Horizontal(g1)
    c: Horizontal(g3)
    c: Equal(g4,g5)
    c: Equal(g5,g6)
    c: Equal(g6,g7)
    c: Coincident(g8,g9)
    c: Coincident(g9,g10)
    c: Coincident(g10,g11)
    c: Coincident(g11,g8)
    c: Coincident(g8,g4)
    c: Coincident(g9,g5)
    c: Coincident(g10,g6)
    c: Coincident(g11,g7)
    c: PointOnObject(g12,g0)
    c: PointOnObject(g12,g3)
    c: PointOnObject(g13,g1)
    c: PointOnObject(g13,g2)
    c: Distance(g0,g2) = 40
    c: Distance(g1,g3) = 40
    c: Radius(g5) = 2
    c: Coincident(g12,g-1)
FEATURE [PartDesign::Pad] Pad011
  Direction = (0,-1,2e-16)
  Length = 400
  Length2 = 10
  Placement = pos=(0,0,0) rot=(1,0,0;1.5708rad)
  Profile = -> Sketch012
  ReferenceAxis = -> Sketch012 [N_Axis]
  Suppressed = false
  Type = 0
FEATURE [PartDesign::Body] Body010
  AllowCompound = false
  Group = -> [Sketch012,Pad011]
  Origin = -> Origin021
  Placement = pos=(-14,-400,-400) rot=(0.707107,-0.707107,0;3.14159rad)
  Tip = -> Pad011
FEATURE [Sketcher::SketchObject] Sketch013
  ArcFitTolerance = 1e-06
  AttachmentSupport = -> [XZ_Plane022]
  FullyConstrained = true
  MakeInternals = false
  MapMode = 5
  Placement = pos=(0,0,0) rot=(1,0,0;1.5708rad)
  sketch-geometry (14):
    g0: LineSegment StartX=0 StartY=-2 StartZ=0 EndX=0 EndY=-38 EndZ=0
    g1: LineSegment StartX=2 StartY=-40 StartZ=0 EndX=38 EndY=-40 EndZ=0
    g2: LineSegment StartX=40 StartY=-38 StartZ=0 EndX=40 EndY=-2 EndZ=0
    g3: LineSegment StartX=38 StartY=0 StartZ=0 EndX=2 EndY=0 EndZ=0
    g4: ArcOfCircle CenterX=2 CenterY=-2 CenterZ=0 NormalX=0 NormalY=0 NormalZ=1 AngleXU=0 Radius=2 StartAngle=1.5708 EndAngle=3.14159
    g5: ArcOfCircle CenterX=2 CenterY=-38 CenterZ=0 NormalX=0 NormalY=0 NormalZ=1 AngleXU=0 Radius=2 StartAngle=3.14159 EndAngle=4.71239
    g6: ArcOfCircle CenterX=38 CenterY=-38 CenterZ=0 NormalX=0 NormalY=0 NormalZ=1 AngleXU=0 Radius=2 StartAngle=4.71239 EndAngle=6.28319
    g7: ArcOfCircle CenterX=38 CenterY=-2 CenterZ=0 NormalX=0 NormalY=0 NormalZ=1 AngleXU=0 Radius=2 StartAngle=0 EndAngle=1.5708
    g8: LineSegment StartX=2 StartY=-2 StartZ=0 EndX=2 EndY=-38 EndZ=0
    g9: LineSegment StartX=2 StartY=-38 StartZ=0 EndX=38 EndY=-38 EndZ=0
    g10: LineSegment StartX=38 StartY=-38 StartZ=0 EndX=38 EndY=-2 EndZ=0
    g11: LineSegment StartX=38 StartY=-2 StartZ=0 EndX=2 EndY=-2 EndZ=0
    g12: GeomPoint [constr] X=0 Y=0 Z=0
    g13: GeomPoint [constr] X=40 Y=-40 Z=0
  constraints (31):
    c: Tangent(g0,g4) = -1.5708
    c: Tangent(g0,g5) = -1.5708
    c: Tangent(g1,g5) = -1.5708
    c: Tangent(g1,g6) = -1.5708
    c: Tangent(g2,g6) = -1.5708
    c: Tangent(g2,g7) = -1.5708
    c: Tangent(g3,g7) = -1.5708
    c: Tangent(g3,g4) = -1.5708
    c: Vertical(g0)
    c: Vertical(g2)
    c: Horizontal(g1)
    c: Horizontal(g3)
    c: Equal(g4,g5)
    c: Equal(g5,g6)
    c: Equal(g6,g7)
    c: Coincident(g8,g9)
    c: Coincident(g9,g10)
    c: Coincident(g10,g11)
    c: Coincident(g11,g8)
    c: Coincident(g8,g4)
    c: Coincident(g9,g5)
    c: Coincident(g10,g6)
    c: Coincident(g11,g7)
    c: PointOnObject(g12,g0)
    c: PointOnObject(g12,g3)
    c: PointOnObject(g13,g1)
    c: PointOnObject(g13,g2)
    c: Distance(g0,g2) = 40
    c: Distance(g1,g3) = 40
    c: Radius(g5) = 2
    c: Coincident(g12,g-1)
FEATURE [PartDesign::Pad] Pad012
  Direction = (0,-1,2e-16)
  Length = 400
  Length2 = 10
  Placement = pos=(0,0,0) rot=(1,0,0;1.5708rad)
  Profile = -> Sketch013
  ReferenceAxis = -> Sketch013 [N_Axis]
  Suppressed = false
  Type = 0
FEATURE [PartDesign::Body] Body011
  AllowCompound = false
  Group = -> [Sketch013,Pad012]
  Origin = -> Origin022
  Placement = pos=(-14,40,-400) rot=(-0.707107,0.707107,0;3.14159rad)
  Tip = -> Pad012
FEATURE [Part::Feature] Part__Feature016  label="NEMA23 - PSM57HS2A54-2P003"
  Placement = pos=(713,33,35) rot=(0,0,1;3.14159rad)
  shape: bbox 56.89 x 76.8 x 56.89 mm, 146 faces, 2 solids (baked)
FEATURE [App::Part] Part  label="steppers"
  Group = -> [Part__Feature001,Part__Feature,Part__Feature002,Part__Feature016]
  Origin = -> Origin001
  Placement = pos=(-360,0,0) rot=(0,0,1;0rad)
FEATURE [Part::FeaturePython] ThreadedRod001  label="8x400-ThreadedRod001"  # WARN: FeaturePython — macro-defined, semantics opaque (R4)
  Diameter = 29
  DiameterCustom = 8
  Invert = false
  LeftHanded = false
  Length = 400
  MatchOuter = false
  OffsetAngle = 0
  PitchCustom = 2
  Placement = pos=(353,-418,35) rot=(1,0,0;1.5708rad)
  Thread = true
  Type = 4
FEATURE [Part::Feature] Part__Feature017  label="Coupler 6.35-8mm Without Screw001"
  Placement = pos=(334,0,0) rot=(0,0,1;0rad)
  shape: bbox 20.93 x 20.57 x 29.69 mm, 170 faces (baked)
FEATURE [App::Part] Coupler_6_35_8mm_Without_Screw  label="Coupler 6.35-8mm"
  Group = -> [Part__Feature013,Part__Feature017]
  Origin = -> Origin014
  Placement = pos=(19,-19,35) rot=(1,0,0;4.71239rad)
FEATURE [App::Part] Part008  label="SC8UU bearing supports"
  Origin = -> Origin024
FEATURE [Sketcher::SketchObject] Sketch017
  ArcFitTolerance = 1e-06
  AttachmentSupport = -> [XZ_Plane025]
  FullyConstrained = true
  MakeInternals = false
  MapMode = 5
  Placement = pos=(0,0,0) rot=(1,0,0;1.5708rad)
  sketch-geometry (14):
    g0: LineSegment StartX=0 StartY=-2 StartZ=0 EndX=0 EndY=-38 EndZ=0
    g1: LineSegment StartX=2 StartY=-40 StartZ=0 EndX=38 EndY=-40 EndZ=0
    g2: LineSegment StartX=40 StartY=-38 StartZ=0 EndX=40 EndY=-2 EndZ=0
    g3: LineSegment StartX=38 StartY=0 StartZ=0 EndX=2 EndY=0 EndZ=0
    g4: ArcOfCircle CenterX=2 CenterY=-2 CenterZ=0 NormalX=0 NormalY=0 NormalZ=1 AngleXU=0 Radius=2 StartAngle=1.5708 EndAngle=3.14159
    g5: ArcOfCircle CenterX=2 CenterY=-38 CenterZ=0 NormalX=0 NormalY=0 NormalZ=1 AngleXU=0 Radius=2 StartAngle=3.14159 EndAngle=4.71239
    g6: ArcOfCircle CenterX=38 CenterY=-38 CenterZ=0 NormalX=0 NormalY=0 NormalZ=1 AngleXU=0 Radius=2 StartAngle=4.71239 EndAngle=6.28319
    g7: ArcOfCircle CenterX=38 CenterY=-2 CenterZ=0 NormalX=0 NormalY=0 NormalZ=1 AngleXU=0 Radius=2 StartAngle=0 EndAngle=1.5708
    g8: LineSegment StartX=2 StartY=-2 StartZ=0 EndX=2 EndY=-38 EndZ=0
    g9: LineSegment StartX=2 StartY=-38 StartZ=0 EndX=38 EndY=-38 EndZ=0
    g10: LineSegment StartX=38 StartY=-38 StartZ=0 EndX=38 EndY=-2 EndZ=0
    g11: LineSegment StartX=38 StartY=-2 StartZ=0 EndX=2 EndY=-2 EndZ=0
    g12: GeomPoint [constr] X=0 Y=0 Z=0
    g13: GeomPoint [constr] X=40 Y=-40 Z=0
  constraints (31):
    c: Tangent(g0,g4) = -1.5708
    c: Tangent(g0,g5) = -1.5708
    c: Tangent(g1,g5) = -1.5708
    c: Tangent(g1,g6) = -1.5708
    c: Tangent(g2,g6) = -1.5708
    c: Tangent(g2,g7) = -1.5708
    c: Tangent(g3,g7) = -1.5708
    c: Tangent(g3,g4) = -1.5708
    c: Vertical(g0)
    c: Vertical(g2)
    c: Horizontal(g1)
    c: Horizontal(g3)
    c: Equal(g4,g5)
    c: Equal(g5,g6)
    c: Equal(g6,g7)
    c: Coincident(g8,g9)
    c: Coincident(g9,g10)
    c: Coincident(g10,g11)
    c: Coincident(g11,g8)
    c: Coincident(g8,g4)
    c: Coincident(g9,g5)
    c: Coincident(g10,g6)
    c: Coincident(g11,g7)
    c: PointOnObject(g12,g0)
    c: PointOnObject(g12,g3)
    c: PointOnObject(g13,g1)
    c: PointOnObject(g13,g2)
    c: Distance(g0,g2) = 40
    c: Distance(g1,g3) = 40
    c: Radius(g5) = 2
    c: Coincident(g12,g-1)
FEATURE [PartDesign::Pad] Pad015
  Direction = (0,-1,2e-16)
  Length = 400
  Length2 = 10
  Placement = pos=(0,0,0) rot=(1,0,0;1.5708rad)
  Profile = -> Sketch017
  ReferenceAxis = -> Sketch017 [N_Axis]
  Suppressed = false
  Type = 0
FEATURE [PartDesign::Body] Body013
  AllowCompound = false
  Group = -> [Sketch017,Pad015]
  Origin = -> Origin025
  Placement = pos=(386,-400,-16.5) rot=(0,0,1;4.71239rad)
  Tip = -> Pad015
FEATURE [Sketcher::SketchObject] Sketch018
  ArcFitTolerance = 1e-06
  AttachmentSupport = -> [XZ_Plane026]
  FullyConstrained = true
  MakeInternals = false
  MapMode = 5
  Placement = pos=(0,0,0) rot=(1,0,0;1.5708rad)
  sketch-geometry (14):
    g0: LineSegment StartX=0 StartY=-2 StartZ=0 EndX=0 EndY=-38 EndZ=0
    g1: LineSegment StartX=2 StartY=-40 StartZ=0 EndX=38 EndY=-40 EndZ=0
    g2: LineSegment StartX=40 StartY=-38 StartZ=0 EndX=40 EndY=-2 EndZ=0
    g3: LineSegment StartX=38 StartY=0 StartZ=0 EndX=2 EndY=0 EndZ=0
    g4: ArcOfCircle CenterX=2 CenterY=-2 CenterZ=0 NormalX=0 NormalY=0 NormalZ=1 AngleXU=0 Radius=2 StartAngle=1.5708 EndAngle=3.14159
    g5: ArcOfCircle CenterX=2 CenterY=-38 CenterZ=0 NormalX=0 NormalY=0 NormalZ=1 AngleXU=0 Radius=2 StartAngle=3.14159 EndAngle=4.71239
    g6: ArcOfCircle CenterX=38 CenterY=-38 CenterZ=0 NormalX=0 NormalY=0 NormalZ=1 AngleXU=0 Radius=2 StartAngle=4.71239 EndAngle=6.28319
    g7: ArcOfCircle CenterX=38 CenterY=-2 CenterZ=0 NormalX=0 NormalY=0 NormalZ=1 AngleXU=0 Radius=2 StartAngle=0 EndAngle=1.5708
    g8: LineSegment StartX=2 StartY=-2 StartZ=0 EndX=2 EndY=-38 EndZ=0
    g9: LineSegment StartX=2 StartY=-38 StartZ=0 EndX=38 EndY=-38 EndZ=0
    g10: LineSegment StartX=38 StartY=-38 StartZ=0 EndX=38 EndY=-2 EndZ=0
    g11: LineSegment StartX=38 StartY=-2 StartZ=0 EndX=2 EndY=-2 EndZ=0
    g12: GeomPoint [constr] X=0 Y=0 Z=0
    g13: GeomPoint [constr] X=40 Y=-40 Z=0
  constraints (31):
    c: Tangent(g0,g4) = -1.5708
    c: Tangent(g0,g5) = -1.5708
    c: Tangent(g1,g5) = -1.5708
    c: Tangent(g1,g6) = -1.5708
    c: Tangent(g2,g6) = -1.5708
    c: Tangent(g2,g7) = -1.5708
    c: Tangent(g3,g7) = -1.5708
    c: Tangent(g3,g4) = -1.5708
    c: Vertical(g0)
    c: Vertical(g2)
    c: Horizontal(g1)
    c: Horizontal(g3)
    c: Equal(g4,g5)
    c: Equal(g5,g6)
    c: Equal(g6,g7)
    c: Coincident(g8,g9)
    c: Coincident(g9,g10)
    c: Coincident(g10,g11)
    c: Coincident(g11,g8)
    c: Coincident(g8,g4)
    c: Coincident(g9,g5)
    c: Coincident(g10,g6)
    c: Coincident(g11,g7)
    c: PointOnObject(g12,g0)
    c: PointOnObject(g12,g3)
    c: PointOnObject(g13,g1)
    c: PointOnObject(g13,g2)
    c: Distance(g0,g2) = 40
    c: Distance(g1,g3) = 40
    c: Radius(g5) = 2
    c: Coincident(g12,g-1)
FEATURE [PartDesign::Pad] Pad016
  Direction = (0,-1,2e-16)
  Length = 400
  Length2 = 10
  Placement = pos=(0,0,0) rot=(1,0,0;1.5708rad)
  Profile = -> Sketch018
  ReferenceAxis = -> Sketch018 [N_Axis]
  Suppressed = false
  Type = 0
FEATURE [PartDesign::Body] Body014
  AllowCompound = false
  Group = -> [Sketch018,Pad016]
  Origin = -> Origin026
  Placement = pos=(-14,0,0) rot=(0,0,1;0rad)
  Tip = -> Pad016
FEATURE [Sketcher::SketchObject] Sketch019
  ArcFitTolerance = 1e-06
  AttachmentSupport = -> [XZ_Plane027]
  FullyConstrained = true
  MakeInternals = false
  MapMode = 5
  Placement = pos=(0,0,0) rot=(1,0,0;1.5708rad)
  sketch-geometry (14):
    g0: LineSegment StartX=0 StartY=-2 StartZ=0 EndX=0 EndY=-38 EndZ=0
    g1: LineSegment StartX=2 StartY=-40 StartZ=0 EndX=38 EndY=-40 EndZ=0
    g2: LineSegment StartX=40 StartY=-38 StartZ=0 EndX=40 EndY=-2 EndZ=0
    g3: LineSegment StartX=38 StartY=0 StartZ=0 EndX=2 EndY=0 EndZ=0
    g4: ArcOfCircle CenterX=2 CenterY=-2 CenterZ=0 NormalX=0 NormalY=0 NormalZ=1 AngleXU=0 Radius=2 StartAngle=1.5708 EndAngle=3.14159
    g5: ArcOfCircle CenterX=2 CenterY=-38 CenterZ=0 NormalX=0 NormalY=0 NormalZ=1 AngleXU=0 Radius=2 StartAngle=3.14159 EndAngle=4.71239
    g6: ArcOfCircle CenterX=38 CenterY=-38 CenterZ=0 NormalX=0 NormalY=0 NormalZ=1 AngleXU=0 Radius=2 StartAngle=4.71239 EndAngle=6.28319
    g7: ArcOfCircle CenterX=38 CenterY=-2 CenterZ=0 NormalX=0 NormalY=0 NormalZ=1 AngleXU=0 Radius=2 StartAngle=0 EndAngle=1.5708
    g8: LineSegment StartX=2 StartY=-2 StartZ=0 EndX=2 EndY=-38 EndZ=0
    g9: LineSegment StartX=2 StartY=-38 StartZ=0 EndX=38 EndY=-38 EndZ=0
    g10: LineSegment StartX=38 StartY=-38 StartZ=0 EndX=38 EndY=-2 EndZ=0
    g11: LineSegment StartX=38 StartY=-2 StartZ=0 EndX=2 EndY=-2 EndZ=0
    g12: GeomPoint [constr] X=0 Y=0 Z=0
    g13: GeomPoint [constr] X=40 Y=-40 Z=0
  constraints (31):
    c: Tangent(g0,g4) = -1.5708
    c: Tangent(g0,g5) = -1.5708
    c: Tangent(g1,g5) = -1.5708
    c: Tangent(g1,g6) = -1.5708
    c: Tangent(g2,g6) = -1.5708
    c: Tangent(g2,g7) = -1.5708
    c: Tangent(g3,g7) = -1.5708
    c: Tangent(g3,g4) = -1.5708
    c: Vertical(g0)
    c: Vertical(g2)
    c: Horizontal(g1)
    c: Horizontal(g3)
    c: Equal(g4,g5)
    c: Equal(g5,g6)
    c: Equal(g6,g7)
    c: Coincident(g8,g9)
    c: Coincident(g9,g10)
    c: Coincident(g10,g11)
    c: Coincident(g11,g8)
    c: Coincident(g8,g4)
    c: Coincident(g9,g5)
    c: Coincident(g10,g6)
    c: Coincident(g11,g7)
    c: PointOnObject(g12,g0)
    c: PointOnObject(g12,g3)
    c: PointOnObject(g13,g1)
    c: PointOnObject(g13,g2)
    c: Distance(g0,g2) = 40
    c: Distance(g1,g3) = 40
    c: Radius(g5) = 2
    c: Coincident(g12,g-1)
FEATURE [PartDesign::Pad] Pad017
  Direction = (0,-1,2e-16)
  Length = 400
  Length2 = 10
  Placement = pos=(0,0,0) rot=(1,0,0;1.5708rad)
  Profile = -> Sketch019
  ReferenceAxis = -> Sketch019 [N_Axis]
  Suppressed = false
  Type = 0
FEATURE [PartDesign::Body] Body015
  AllowCompound = false
  Group = -> [Sketch019,Pad017]
  Origin = -> Origin027
  Placement = pos=(386,0,0) rot=(0,0,1;0rad)
  Tip = -> Pad017
FEATURE [Part::Feature] Part__Feature020  label="Anti-Backlash_Nut_TR8x2"
  shape: bbox 13.31 x 19.2 x 12.91 mm, 12 faces (baked)
FEATURE [Part::Feature] Part__Feature021  label="Anti-Backlash_Nut_TR8x003"
  shape: bbox 22 x 16.19 x 22 mm, 78 faces (baked)
FEATURE [Part::Feature] Part__Feature022  label="Anti-Backlash_Nut_TR8x004"
  shape: bbox 14 x 15.64 x 14 mm, 59 faces (baked)
FEATURE [Sketcher::SketchObject] Sketch020
  ArcFitTolerance = 1e-06
  AttachmentSupport = -> [XZ_Plane029]
  FullyConstrained = true
  MakeInternals = false
  MapMode = 5
  Placement = pos=(0,0,0) rot=(1,0,0;1.5708rad)
  sketch-geometry (14):
    g0: LineSegment StartX=0 StartY=-2 StartZ=0 EndX=0 EndY=-38 EndZ=0
    g1: LineSegment StartX=2 StartY=-40 StartZ=0 EndX=38 EndY=-40 EndZ=0
    g2: LineSegment StartX=40 StartY=-38 StartZ=0 EndX=40 EndY=-2 EndZ=0
    g3: LineSegment StartX=38 StartY=0 StartZ=0 EndX=2 EndY=0 EndZ=0
    g4: ArcOfCircle CenterX=2 CenterY=-2 CenterZ=0 NormalX=0 NormalY=0 NormalZ=1 AngleXU=0 Radius=2 StartAngle=1.5708 EndAngle=3.14159
    g5: ArcOfCircle CenterX=2 CenterY=-38 CenterZ=0 NormalX=0 NormalY=0 NormalZ=1 AngleXU=0 Radius=2 StartAngle=3.14159 EndAngle=4.71239
    g6: ArcOfCircle CenterX=38 CenterY=-38 CenterZ=0 NormalX=0 NormalY=0 NormalZ=1 AngleXU=0 Radius=2 StartAngle=4.71239 EndAngle=6.28319
    g7: ArcOfCircle CenterX=38 CenterY=-2 CenterZ=0 NormalX=0 NormalY=0 NormalZ=1 AngleXU=0 Radius=2 StartAngle=0 EndAngle=1.5708
    g8: LineSegment StartX=2 StartY=-2 StartZ=0 EndX=2 EndY=-38 EndZ=0
    g9: LineSegment StartX=2 StartY=-38 StartZ=0 EndX=38 EndY=-38 EndZ=0
    g10: LineSegment StartX=38 StartY=-38 StartZ=0 EndX=38 EndY=-2 EndZ=0
    g11: LineSegment StartX=38 StartY=-2 StartZ=0 EndX=2 EndY=-2 EndZ=0
    g12: GeomPoint [constr] X=0 Y=0 Z=0
    g13: GeomPoint [constr] X=40 Y=-40 Z=0
  constraints (31):
    c: Tangent(g0,g4) = -1.5708
    c: Tangent(g0,g5) = -1.5708
    c: Tangent(g1,g5) = -1.5708
    c: Tangent(g1,g6) = -1.5708
    c: Tangent(g2,g6) = -1.5708
    c: Tangent(g2,g7) = -1.5708
    c: Tangent(g3,g7) = -1.5708
    c: Tangent(g3,g4) = -1.5708
    c: Vertical(g0)
    c: Vertical(g2)
    c: Horizontal(g1)
    c: Horizontal(g3)
    c: Equal(g4,g5)
    c: Equal(g5,g6)
    c: Equal(g6,g7)
    c: Coincident(g8,g9)
    c: Coincident(g9,g10)
    c: Coincident(g10,g11)
    c: Coincident(g11,g8)
    c: Coincident(g8,g4)
    c: Coincident(g9,g5)
    c: Coincident(g10,g6)
    c: Coincident(g11,g7)
    c: PointOnObject(g12,g0)
    c: PointOnObject(g12,g3)
    c: PointOnObject(g13,g1)
    c: PointOnObject(g13,g2)
    c: Distance(g0,g2) = 40
    c: Distance(g1,g3) = 40
    c: Radius(g5) = 2
    c: Coincident(g12,g-1)
FEATURE [PartDesign::Pad] Pad018
  Direction = (0,-1,2e-16)
  Length = 400
  Length2 = 10
  Placement = pos=(0,0,0) rot=(1,0,0;1.5708rad)
  Profile = -> Sketch020
  ReferenceAxis = -> Sketch020 [N_Axis]
  Suppressed = false
  Type = 0
FEATURE [PartDesign::Body] Body016
  AllowCompound = false
  Group = -> [Sketch020,Pad018]
  Origin = -> Origin029
  Placement = pos=(386,-400,-400) rot=(-1,0,0;3.14159rad)
  Tip = -> Pad018
FEATURE [Sketcher::SketchObject] Sketch021
  ArcFitTolerance = 1e-06
  AttachmentSupport = -> [XZ_Plane030]
  FullyConstrained = true
  MakeInternals = false
  MapMode = 5
  Placement = pos=(0,0,0) rot=(1,0,0;1.5708rad)
  sketch-geometry (14):
    g0: LineSegment StartX=0 StartY=-2 StartZ=0 EndX=0 EndY=-38 EndZ=0
    g1: LineSegment StartX=2 StartY=-40 StartZ=0 EndX=38 EndY=-40 EndZ=0
    g2: LineSegment StartX=40 StartY=-38 StartZ=0 EndX=40 EndY=-2 EndZ=0
    g3: LineSegment StartX=38 StartY=0 StartZ=0 EndX=2 EndY=0 EndZ=0
    g4: ArcOfCircle CenterX=2 CenterY=-2 CenterZ=0 NormalX=0 NormalY=0 NormalZ=1 AngleXU=0 Radius=2 StartAngle=1.5708 EndAngle=3.14159
    g5: ArcOfCircle CenterX=2 CenterY=-38 CenterZ=0 NormalX=0 NormalY=0 NormalZ=1 AngleXU=0 Radius=2 StartAngle=3.14159 EndAngle=4.71239
    g6: ArcOfCircle CenterX=38 CenterY=-38 CenterZ=0 NormalX=0 NormalY=0 NormalZ=1 AngleXU=0 Radius=2 StartAngle=4.71239 EndAngle=6.28319
    g7: ArcOfCircle CenterX=38 CenterY=-2 CenterZ=0 NormalX=0 NormalY=0 NormalZ=1 AngleXU=0 Radius=2 StartAngle=0 EndAngle=1.5708
    g8: LineSegment StartX=2 StartY=-2 StartZ=0 EndX=2 EndY=-38 EndZ=0
    g9: LineSegment StartX=2 StartY=-38 StartZ=0 EndX=38 EndY=-38 EndZ=0
    g10: LineSegment StartX=38 StartY=-38 StartZ=0 EndX=38 EndY=-2 EndZ=0
    g11: LineSegment StartX=38 StartY=-2 StartZ=0 EndX=2 EndY=-2 EndZ=0
    g12: GeomPoint [constr] X=0 Y=0 Z=0
    g13: GeomPoint [constr] X=40 Y=-40 Z=0
  constraints (31):
    c: Tangent(g0,g4) = -1.5708
    c: Tangent(g0,g5) = -1.5708
    c: Tangent(g1,g5) = -1.5708
    c: Tangent(g1,g6) = -1.5708
    c: Tangent(g2,g6) = -1.5708
    c: Tangent(g2,g7) = -1.5708
    c: Tangent(g3,g7) = -1.5708
    c: Tangent(g3,g4) = -1.5708
    c: Vertical(g0)
    c: Vertical(g2)
    c: Horizontal(g1)
    c: Horizontal(g3)
    c: Equal(g4,g5)
    c: Equal(g5,g6)
    c: Equal(g6,g7)
    c: Coincident(g8,g9)
    c: Coincident(g9,g10)
    c: Coincident(g10,g11)
    c: Coincident(g11,g8)
    c: Coincident(g8,g4)
    c: Coincident(g9,g5)
    c: Coincident(g10,g6)
    c: Coincident(g11,g7)
    c: PointOnObject(g12,g0)
    c: PointOnObject(g12,g3)
    c: PointOnObject(g13,g1)
    c: PointOnObject(g13,g2)
    c: Distance(g0,g2) = 40
    c: Distance(g1,g3) = 40
    c: Radius(g5) = 2
    c: Coincident(g12,g-1)
FEATURE [PartDesign::Pad] Pad019
  Direction = (0,-1,2e-16)
  Length = 400
  Length2 = 10
  Placement = pos=(0,0,0) rot=(1,0,0;1.5708rad)
  Profile = -> Sketch021
  ReferenceAxis = -> Sketch021 [N_Axis]
  Suppressed = false
  Type = 0
FEATURE [PartDesign::Body] Body017
  AllowCompound = false
  Group = -> [Sketch021,Pad019]
  Origin = -> Origin030
  Placement = pos=(-54,-400,-400) rot=(-1,0,0;3.14159rad)
  Tip = -> Pad019
FEATURE [App::Part] Part007  label="legs"
  Group = -> [Body006,Body008,Body007,Body009,Body010,Body011,Body016,Body017]
  Origin = -> Origin016
FEATURE [Part::Feature] Part__Feature023  label="Anti-Backlash_Nut_TR8x006"
  Placement = pos=(334.293,0,0) rot=(0,0,1;0rad)
  shape: bbox 13.31 x 19.2 x 12.91 mm, 12 faces (baked)
FEATURE [Part::Feature] Part__Feature024  label="Anti-Backlash_Nut_TR8x007"
  Placement = pos=(334.293,0,0) rot=(0,0,1;0rad)
  shape: bbox 22 x 16.19 x 22 mm, 78 faces (baked)
FEATURE [Part::Feature] Part__Feature025  label="Anti-Backlash_Nut_TR8x008"
  Placement = pos=(334.293,0,0) rot=(0,0,1;0rad)
  shape: bbox 14 x 15.64 x 14 mm, 59 faces (baked)
FEATURE [App::Part] Anti_Backlash_Nut_TR8x2  label="Anti-Backlash_Nut_TR8x005"
  Group = -> [Part__Feature020,Part__Feature021,Part__Feature022,Part__Feature023,Part__Feature024,Part__Feature025]
  Origin = -> Origin028
  Placement = pos=(19,-141.5,35) rot=(0,0,1;0rad)
FEATURE [Sketcher::SketchObject] Sketch022
  ArcFitTolerance = 1e-06
  AttachmentSupport = -> [XZ_Plane031]
  FullyConstrained = true
  MakeInternals = false
  MapMode = 5
  Placement = pos=(0,0,0) rot=(1,0,0;1.5708rad)
  sketch-geometry (14):
    g0: LineSegment StartX=0 StartY=-2 StartZ=0 EndX=0 EndY=-38 EndZ=0
    g1: LineSegment StartX=2 StartY=-40 StartZ=0 EndX=38 EndY=-40 EndZ=0
    g2: LineSegment StartX=40 StartY=-38 StartZ=0 EndX=40 EndY=-2 EndZ=0
    g3: LineSegment StartX=38 StartY=0 StartZ=0 EndX=2 EndY=0 EndZ=0
    g4: ArcOfCircle CenterX=2 CenterY=-2 CenterZ=0 NormalX=0 NormalY=0 NormalZ=1 AngleXU=0 Radius=2 StartAngle=1.5708 EndAngle=3.14159
    g5: ArcOfCircle CenterX=2 CenterY=-38 CenterZ=0 NormalX=0 NormalY=0 NormalZ=1 AngleXU=0 Radius=2 StartAngle=3.14159 EndAngle=4.71239
    g6: ArcOfCircle CenterX=38 CenterY=-38 CenterZ=0 NormalX=0 NormalY=0 NormalZ=1 AngleXU=0 Radius=2 StartAngle=4.71239 EndAngle=6.28319
    g7: ArcOfCircle CenterX=38 CenterY=-2 CenterZ=0 NormalX=0 NormalY=0 NormalZ=1 AngleXU=0 Radius=2 StartAngle=0 EndAngle=1.5708
    g8: LineSegment StartX=2 StartY=-2 StartZ=0 EndX=2 EndY=-38 EndZ=0
    g9: LineSegment StartX=2 StartY=-38 StartZ=0 EndX=38 EndY=-38 EndZ=0
    g10: LineSegment StartX=38 StartY=-38 StartZ=0 EndX=38 EndY=-2 EndZ=0
    g11: LineSegment StartX=38 StartY=-2 StartZ=0 EndX=2 EndY=-2 EndZ=0
    g12: GeomPoint [constr] X=0 Y=0 Z=0
    g13: GeomPoint [constr] X=40 Y=-40 Z=0
  constraints (31):
    c: Tangent(g0,g4) = -1.5708
    c: Tangent(g0,g5) = -1.5708
    c: Tangent(g1,g5) = -1.5708
    c: Tangent(g1,g6) = -1.5708
    c: Tangent(g2,g6) = -1.5708
    c: Tangent(g2,g7) = -1.5708
    c: Tangent(g3,g7) = -1.5708
    c: Tangent(g3,g4) = -1.5708
    c: Vertical(g0)
    c: Vertical(g2)
    c: Horizontal(g1)
    c: Horizontal(g3)
    c: Equal(g4,g5)
    c: Equal(g5,g6)
    c: Equal(g6,g7)
    c: Coincident(g8,g9)
    c: Coincident(g9,g10)
    c: Coincident(g10,g11)
    c: Coincident(g11,g8)
    c: Coincident(g8,g4)
    c: Coincident(g9,g5)
    c: Coincident(g10,g6)
    c: Coincident(g11,g7)
    c: PointOnObject(g12,g0)
    c: PointOnObject(g12,g3)
    c: PointOnObject(g13,g1)
    c: PointOnObject(g13,g2)
    c: Distance(g0,g2) = 40
    c: Distance(g1,g3) = 40
    c: Radius(g5) = 2
    c: Coincident(g12,g-1)
FEATURE [PartDesign::Pad] Pad020
  Direction = (0,-1,2e-16)
  Length = 400
  Length2 = 10
  Placement = pos=(0,0,0) rot=(1,0,0;1.5708rad)
  Profile = -> Sketch022
  ReferenceAxis = -> Sketch022 [N_Axis]
  Suppressed = false
  Type = 0
FEATURE [Sketcher::SketchObject] Sketch023
  ArcFitTolerance = 1e-06
  AttachmentSupport = -> [Pad020]
  ExternalGeometry = -> [Pad020]
  FullyConstrained = false
  MakeInternals = false
  MapMode = 5
  Placement = pos=(0,0,0) rot=(0.707107,0,-0.707107;3.14159rad)
  sketch-geometry (2):
    g0: LineSegment [constr] StartX=0 StartY=200 StartZ=0 EndX=40 EndY=200 EndZ=0
    g1: Circle CenterX=20 CenterY=200 CenterZ=0 NormalX=0 NormalY=0 NormalZ=1 AngleXU=0 Radius=3.39501
  constraints (4):
    c: Horizontal(g0)
    c: PointOnObject(g0,g-2)
    c: PointOnObject(g0,g-3)
    c: Distance(g-1,g0) = 200
FEATURE [PartDesign::Pocket] Pocket002  label="rod-hole"
  BaseFeature = -> Pad020
  Direction = (1,0,2e-16)
  Length = 40
  Length2 = 5
  Placement = pos=(0,0,0) rot=(1,0,0;1.5708rad)
  Profile = -> Sketch023
  ReferenceAxis = -> Sketch023 [N_Axis]
  Suppressed = false
  Type = 0
FEATURE [Part::Feature] Part__Feature026  label="Anti-Backlash_Nut_TR8x010"
  shape: bbox 13.31 x 19.2 x 12.91 mm, 12 faces (baked)
FEATURE [Part::Feature] Part__Feature027  label="Anti-Backlash_Nut_TR8x011"
  shape: bbox 22 x 16.19 x 22 mm, 78 faces (baked)
FEATURE [Part::Feature] Part__Feature028  label="Anti-Backlash_Nut_TR8x012"
  shape: bbox 14 x 15.64 x 14 mm, 59 faces (baked)
FEATURE [App::Part] Anti_Backlash_Nut_TR8x003  label="Anti-Backlash_Nut_TR8x009"
  Group = -> [Part__Feature026,Part__Feature027,Part__Feature028]
  Origin = -> Origin032
  Placement = pos=(353,-180.5,35) rot=(0,0,1;3.14159rad)
FEATURE [Sketcher::SketchObject] Sketch024
  ArcFitTolerance = 1e-06
  AttachmentSupport = -> [Pocket002]
  ExternalGeometry = -> [Pocket002]
  FullyConstrained = false
  MakeInternals = false
  MapMode = 5
  Placement = pos=(0,-8.4e-15,-38) rot=(0,0,1;3.14159rad)
  sketch-geometry (9):
    g0: Circle CenterX=-28.25 CenterY=359.5 CenterZ=0 NormalX=0 NormalY=0 NormalZ=1 AngleXU=0 Radius=2
    g1: Circle CenterX=-12.2174 CenterY=359.5 CenterZ=0 NormalX=0 NormalY=0 NormalZ=1 AngleXU=0 Radius=2
    g2: Circle CenterX=-12.2174 CenterY=374.5 CenterZ=0 NormalX=0 NormalY=0 NormalZ=1 AngleXU=0 Radius=2
    g3: Circle CenterX=-28.2001 CenterY=374.5 CenterZ=0 NormalX=0 NormalY=0 NormalZ=1 AngleXU=0 Radius=2
    g4: LineSegment [constr] StartX=-40 StartY=200 StartZ=0 EndX=-10 EndY=200 EndZ=0
    g5: Circle CenterX=-28.25 CenterY=40.5 CenterZ=0 NormalX=0 NormalY=0 NormalZ=1 AngleXU=0 Radius=2
    g6: Circle CenterX=-12.2174 CenterY=40.5 CenterZ=0 NormalX=0 NormalY=0 NormalZ=1 AngleXU=0 Radius=2
    g7: Circle CenterX=-12.2174 CenterY=25.5 CenterZ=0 NormalX=0 NormalY=0 NormalZ=1 AngleXU=0 Radius=2
    g8: Circle CenterX=-28.2001 CenterY=25.5 CenterZ=0 NormalX=0 NormalY=0 NormalZ=1 AngleXU=0 Radius=2
  constraints (16):
    c: Diameter(g0) = 4
    c: Diameter(g1) = 4
    c: Diameter(g2) = 4
    c: Diameter(g3) = 4
    c: Horizontal(g1,g0)
    c: Horizontal(g2,g3)
    c: Vertical(g1,g2)
    c: DistanceY(g0,g3) = 15
    c: Distance(g0,g-4) = 11.75
    c: Distance(g3,g-3) = 25.5
    c: Symmetric(g-4,g-4,g4)
    c: Horizontal(g4)
    c: Diameter(g5) = 4
    c: Diameter(g6) = 4
    c: Diameter(g7) = 4
    c: Diameter(g8) = 4
FEATURE [PartDesign::Pocket] Pocket003
  BaseFeature = -> Pocket002
  Direction = (0,0,-1)
  Length = 50
  Length2 = 5
  Midplane = true
  Placement = pos=(0,0,0) rot=(1,0,0;1.5708rad)
  Profile = -> Sketch024
  ReferenceAxis = -> Sketch024 [N_Axis]
  Suppressed = false
  Type = 0
FEATURE [Part::FeaturePython] Screw001  label="M5x10-Screw"  # WARN: FeaturePython — macro-defined, semantics opaque (R4)
  BaseObject = -> Part002 [Body018.Pocket003.Edge48]
  Diameter = 2
  Invert = false
  LeftHanded = false
  Length = 0
  LengthCustom = 10
  MatchOuter = false
  OffsetAngle = 0
  Placement = pos=(11.5,-153.201,17) rot=(0,0,1;0rad)
  Thread = false
  Type = 36
FEATURE [Part::FeaturePython] Screw002  label="M5x10-Screw394"  # WARN: FeaturePython — macro-defined, semantics opaque (R4)
  BaseObject = -> Part002 [Body018.Pocket003.Edge50]
  Diameter = 2
  Invert = false
  LeftHanded = false
  Length = 0
  LengthCustom = 10
  MatchOuter = false
  OffsetAngle = 0
  Placement = pos=(26.5,-153.201,17) rot=(0,0,1;0rad)
  Thread = false
  Type = 36
FEATURE [Part::FeaturePython] Screw003  label="M5x10-Screw395"  # WARN: FeaturePython — macro-defined, semantics opaque (R4)
  BaseObject = -> Part002 [Body018.Pocket003.Edge51]
  Diameter = 2
  Invert = false
  LeftHanded = false
  Length = 0
  LengthCustom = 10
  MatchOuter = false
  OffsetAngle = 0
  Placement = pos=(26.5,-169.234,17) rot=(0,0,1;0rad)
  Thread = false
  Type = 36
FEATURE [Sketcher::SketchObject] Sketch025
  ArcFitTolerance = 1e-06
  AttachmentSupport = -> [Pocket003]
  ExternalGeometry = -> [Pocket003]
  FullyConstrained = false
  MakeInternals = false
  MapMode = 5
  Placement = pos=(0,0,0) rot=(0,0,1;3.14159rad)
  sketch-geometry (29):
    g0: LineSegment [constr] StartX=-33 StartY=380 StartZ=0 EndX=-33 EndY=354 EndZ=0
    g1: LineSegment [constr] StartX=-33 StartY=354 StartZ=0 EndX=-7 EndY=354 EndZ=0
    g2: LineSegment [constr] StartX=-7 StartY=354 StartZ=0 EndX=-7 EndY=380 EndZ=0
    g3: LineSegment [constr] StartX=-7 StartY=380 StartZ=0 EndX=-33 EndY=380 EndZ=0
    g4: LineSegment StartX=-33 StartY=376.5 StartZ=0 EndX=-33 EndY=357.5 EndZ=0
    g5: LineSegment StartX=-29.5 StartY=354 StartZ=0 EndX=-10.5 EndY=354 EndZ=0
    g6: LineSegment StartX=-7 StartY=357.5 StartZ=0 EndX=-7 EndY=376.5 EndZ=0
    g7: LineSegment StartX=-10.5 StartY=380 StartZ=0 EndX=-29.5 EndY=380 EndZ=0
    g8: ArcOfCircle CenterX=-29.5 CenterY=376.5 CenterZ=0 NormalX=0 NormalY=0 NormalZ=1 AngleXU=0 Radius=3.5 StartAngle=1.5708 EndAngle=3.14159
    g9: ArcOfCircle CenterX=-29.5 CenterY=357.5 CenterZ=0 NormalX=0 NormalY=0 NormalZ=1 AngleXU=0 Radius=3.5 StartAngle=3.14159 EndAngle=4.71239
    g10: ArcOfCircle CenterX=-10.5 CenterY=357.5 CenterZ=0 NormalX=0 NormalY=0 NormalZ=1 AngleXU=0 Radius=3.5 StartAngle=4.71239 EndAngle=6.28319
    g11: ArcOfCircle CenterX=-10.5 CenterY=376.5 CenterZ=0 NormalX=0 NormalY=0 NormalZ=1 AngleXU=0 Radius=3.5 StartAngle=0 EndAngle=1.5708
    g12: GeomPoint [constr] X=-33 Y=380 Z=0
    g13: GeomPoint [constr] X=-7 Y=354 Z=0
    g14: LineSegment [constr] StartX=-38 StartY=200 StartZ=0 EndX=-10 EndY=200 EndZ=0
    g15: LineSegment [constr] StartX=-33 StartY=20 StartZ=0 EndX=-33 EndY=46 EndZ=0
    g16: LineSegment [constr] StartX=-33 StartY=46 StartZ=0 EndX=-7 EndY=46 EndZ=0
    g17: LineSegment [constr] StartX=-7 StartY=46 StartZ=0 EndX=-7 EndY=20 EndZ=0
    g18: LineSegment [constr] StartX=-7 StartY=20 StartZ=0 EndX=-33 EndY=20 EndZ=0
    g19: LineSegment StartX=-33 StartY=23.5 StartZ=0 EndX=-33 EndY=42.5 EndZ=0
    g20: LineSegment StartX=-29.5 StartY=46 StartZ=0 EndX=-10.5 EndY=46 EndZ=0
    g21: LineSegment StartX=-7 StartY=42.5 StartZ=0 EndX=-7 EndY=23.5 EndZ=0
    g22: LineSegment StartX=-10.5 StartY=20 StartZ=0 EndX=-29.5 EndY=20 EndZ=0
    g23: ArcOfCircle CenterX=-29.5 CenterY=23.5 CenterZ=0 NormalX=0 NormalY=0 NormalZ=1 AngleXU=0 Radius=3.5 StartAngle=3.14159 EndAngle=4.71239
    g24: ArcOfCircle CenterX=-29.5 CenterY=42.5 CenterZ=0 NormalX=0 NormalY=0 NormalZ=1 AngleXU=0 Radius=3.5 StartAngle=1.5708 EndAngle=3.14159
    g25: ArcOfCircle CenterX=-10.5 CenterY=42.5 CenterZ=0 NormalX=0 NormalY=0 NormalZ=1 AngleXU=0 Radius=3.5 StartAngle=0 EndAngle=1.5708
    g26: ArcOfCircle CenterX=-10.5 CenterY=23.5 CenterZ=0 NormalX=0 NormalY=0 NormalZ=1 AngleXU=0 Radius=3.5 StartAngle=4.71239 EndAngle=6.28319
    g27: GeomPoint [constr] X=-33 Y=20 Z=0
    g28: GeomPoint [constr] X=-7 Y=46 Z=0
  constraints (68):
    c: Coincident(g0,g1)
    c: Coincident(g1,g2)
    c: Coincident(g2,g3)
    c: Coincident(g3,g0)
    c: Vertical(g0)
    c: Vertical(g2)
    c: Horizontal(g1)
    c: Horizontal(g3)
    c: Distance(g0,g2) = 26
    c: Distance(g1,g3) = 26
    c: Distance(g-5,g3) = 20
    c: DistanceX(g-5,g0) = 5
    c: Tangent(g4,g8) = -1.5708
    c: Tangent(g4,g9) = -1.5708
    c: Tangent(g5,g9) = -1.5708
    c: Tangent(g5,g10) = -1.5708
    c: Tangent(g6,g10) = -1.5708
    c: Tangent(g6,g11) = -1.5708
    c: Tangent(g7,g11) = -1.5708
    c: Tangent(g7,g8) = -1.5708
    c: Vertical(g4)
    c: Vertical(g6)
    c: Horizontal(g5)
    c: Horizontal(g7)
    c: Equal(g8,g9)
    c: Equal(g9,g10)
    c: Equal(g10,g11)
    c: PointOnObject(g12,g4)
    c: PointOnObject(g12,g7)
    c: PointOnObject(g13,g5)
    c: PointOnObject(g13,g6)
    c: Radius(g9) = 3.5
    c: Coincident(g12,g0)
    c: Coincident(g13,g1)
    c: Symmetric(g-3,g-3,g14)
    c: Horizontal(g14)
    c: Coincident(g15,g16)
    c: Coincident(g16,g17)
    c: Coincident(g17,g18)
    c: Coincident(g18,g15)
    c: Vertical(g15)
    c: Vertical(g17)
    c: Horizontal(g16)
    c: Horizontal(g18)
    c: Distance(g15,g17) = 26
    c: Distance(g16,g18) = 26
    c: Tangent(g19,g23) = 1.5708
    c: Tangent(g19,g24) = 1.5708
    c: Tangent(g20,g24) = 1.5708
    c: Tangent(g20,g25) = 1.5708
    c: Tangent(g21,g25) = 1.5708
    c: Tangent(g21,g26) = 1.5708
    c: Tangent(g22,g26) = 1.5708
    c: Tangent(g22,g23) = 1.5708
    c: Vertical(g19)
    c: Vertical(g21)
    c: Horizontal(g20)
    c: Horizontal(g22)
    c: Equal(g23,g24)
    c: Equal(g24,g25)
    c: Equal(g25,g26)
    c: PointOnObject(g27,g19)
    c: PointOnObject(g27,g22)
    c: PointOnObject(g28,g20)
    c: PointOnObject(g28,g21)
    c: Radius(g24) = 3.5
    c: Coincident(g27,g15)
    c: Coincident(g28,g16)
FEATURE [PartDesign::Pocket] Pocket004
  BaseFeature = -> Pocket003
  Direction = (0,0,-1)
  Length = 5
  Length2 = 5
  Placement = pos=(0,0,0) rot=(1,0,0;1.5708rad)
  Profile = -> Sketch025
  ReferenceAxis = -> Sketch025 [N_Axis]
  Suppressed = false
  Type = 0
FEATURE [Part::FeaturePython] Screw  label="M5x10-Screw396"  # WARN: FeaturePython — macro-defined, semantics opaque (R4)
  BaseObject = -> Part002 [Body018.Pocket004.Edge57]
  Diameter = 2
  Invert = false
  LeftHanded = false
  Length = 0
  LengthCustom = 10
  MatchOuter = false
  OffsetAngle = 0
  Placement = pos=(11.5,-169.184,17) rot=(0,0,1;0rad)
  Thread = false
  Type = 36
FEATURE [Sketcher::SketchObject] Sketch026
  ArcFitTolerance = 1e-06
  AttachmentSupport = -> [Pocket004]
  ExternalGeometry = -> [Pocket004]
  FullyConstrained = false
  MakeInternals = false
  MapMode = 5
  Placement = pos=(40,0,0) rot=(0.707107,0,0.707107;3.14159rad)
  sketch-geometry (6):
    g0: LineSegment [constr] StartX=-38 StartY=200 StartZ=0 EndX=2 EndY=200 EndZ=0
    g1: Circle [constr] CenterX=-14.5 CenterY=200 CenterZ=0 NormalX=0 NormalY=0 NormalZ=1 AngleXU=0 Radius=8
    g2: Circle CenterX=-14.5 CenterY=192 CenterZ=0 NormalX=0 NormalY=0 NormalZ=1 AngleXU=0 Radius=2
    g3: Circle CenterX=-14.5 CenterY=208 CenterZ=0 NormalX=0 NormalY=0 NormalZ=1 AngleXU=0 Radius=2
    g4: Circle CenterX=-6.5 CenterY=200 CenterZ=0 NormalX=0 NormalY=0 NormalZ=1 AngleXU=0 Radius=2
    g5: Circle CenterX=-22.5 CenterY=200 CenterZ=0 NormalX=0 NormalY=0 NormalZ=1 AngleXU=0 Radius=2
  constraints (16):
    c: Distance(g0) = 40
    c: Symmetric(g-3,g-3,g0)
    c: Horizontal(g0)
    c: Diameter(g1) = 16
    c: Diameter(g2) = 4
    c: PointOnObject(g2,g1)
    c: Diameter(g3) = 4
    c: PointOnObject(g3,g1)
    c: Diameter(g4) = 4
    c: PointOnObject(g4,g1)
    c: Diameter(g5) = 4
    c: PointOnObject(g5,g1)
    c: Distance(g1,g-3) = 23.5
    c: Distance(g1,g-1) = 200
    c: DistanceX(g5,g4) = 16
    c: DistanceY(g2,g3) = 16
FEATURE [PartDesign::Pocket] Pocket005
  BaseFeature = -> Pocket004
  Direction = (-1,0,2e-16)
  Length = 40
  Length2 = 5
  Placement = pos=(0,0,0) rot=(1,0,0;1.5708rad)
  Profile = -> Sketch026
  ReferenceAxis = -> Sketch026 [N_Axis]
  Suppressed = false
  Type = 0
FEATURE [Part::FeaturePython] Screw004  label="M4x10-Screw"  # WARN: FeaturePython — macro-defined, semantics opaque (R4)
  BaseObject = -> Anti_Backlash_Nut_TR8x2 [Part__Feature021.Edge158]
  Diameter = 1
  Invert = false
  LeftHanded = false
  Length = 0
  LengthCustom = 10
  MatchOuter = false
  OffsetAngle = 0
  Placement = pos=(19,-137.6,43) rot=(-1,0,0;1.5708rad)
  Thread = false
  Type = 36
FEATURE [PartDesign::Pocket] Pocket006  label="small-holes"
  BaseFeature = -> Pocket005
  Direction = (-1,0,2e-16)
  Length = 50
  Length2 = 5
  Placement = pos=(0,0,0) rot=(1,0,0;1.5708rad)
  Profile = -> Sketch026
  ReferenceAxis = -> Sketch026 [N_Axis]
  Suppressed = false
  Type = 0
FEATURE [PartDesign::Body] Body018
  AllowCompound = false
  Group = -> [Sketch022,Pad020,Sketch023,Pocket002,Sketch024,Pocket003,Sketch025,Pocket004,Sketch026,Pocket005,Pocket006]
  Origin = -> Origin031
  Placement = pos=(386,-140.984,55) rot=(0,0,1;4.71239rad)
  Tip = -> Pocket006
FEATURE [Part::FeaturePython] Screw005  label="M4x10-Screw029"  # WARN: FeaturePython — macro-defined, semantics opaque (R4)
  BaseObject = -> Anti_Backlash_Nut_TR8x2 [Part__Feature021.Edge152]
  Diameter = 1
  Invert = false
  LeftHanded = false
  Length = 0
  LengthCustom = 10
  MatchOuter = false
  OffsetAngle = 0
  Placement = pos=(11,-137.6,35) rot=(-1,0,0;1.5708rad)
  Thread = false
  Type = 36
FEATURE [Part::FeaturePython] Screw006  label="M4x10-Screw002"  # WARN: FeaturePython — macro-defined, semantics opaque (R4)
  BaseObject = -> Anti_Backlash_Nut_TR8x2 [Part__Feature021.Edge154]
  Diameter = 1
  Invert = false
  LeftHanded = false
  Length = 0
  LengthCustom = 10
  MatchOuter = false
  OffsetAngle = 0
  Placement = pos=(19,-137.6,27) rot=(-1,0,0;1.5708rad)
  Thread = false
  Type = 36
FEATURE [Part::FeaturePython] Screw007  label="M4x10-Screw003"  # WARN: FeaturePython — macro-defined, semantics opaque (R4)
  BaseObject = -> Anti_Backlash_Nut_TR8x2 [Part__Feature021.Edge28]
  Diameter = 1
  Invert = false
  LeftHanded = false
  Length = 0
  LengthCustom = 10
  MatchOuter = false
  OffsetAngle = 0
  Placement = pos=(27,-137.6,35) rot=(-1,0,0;1.5708rad)
  Thread = false
  Type = 36
FEATURE [Part::Feature] Part__Feature032  label="Round Flange Trapezoidal Tr8"
  Placement = pos=(19,-235,35) rot=(1,0,0;1.5708rad)
  shape: bbox 22 x 15 x 22 mm, 21 faces (baked)
FEATURE [App::Part] Part009  label="tr8 Flange"
  Group = -> [Part__Feature032]
  Origin = -> Origin033
FEATURE [Part::FeaturePython] Screw013  label="M4x10-Screw025"  # WARN: FeaturePython — macro-defined, semantics opaque (R4)
  BaseObject = -> Anti_Backlash_Nut_TR8x003 [Part__Feature030.Edge154]
  Diameter = 1
  Invert = false
  LeftHanded = false
  Length = 0
  LengthCustom = 10
  MatchOuter = false
  OffsetAngle = 0
  Placement = pos=(18.7069,-184.4,27) rot=(1,0,0;1.5708rad)
  Thread = false
  Type = 36
FEATURE [Part::FeaturePython] Screw012  label="M4x10-Screw026"  # WARN: FeaturePython — macro-defined, semantics opaque (R4)
  BaseObject = -> Anti_Backlash_Nut_TR8x003 [Part__Feature030.Edge28]
  Diameter = 1
  Invert = false
  LeftHanded = false
  Length = 0
  LengthCustom = 10
  MatchOuter = false
  OffsetAngle = 0
  Placement = pos=(10.7069,-184.4,35) rot=(1,0,0;1.5708rad)
  Thread = false
  Type = 36
FEATURE [Part::FeaturePython] Screw014  label="M4x10-Screw027"  # WARN: FeaturePython — macro-defined, semantics opaque (R4)
  BaseObject = -> Anti_Backlash_Nut_TR8x003 [Part__Feature030.Edge152]
  Diameter = 1
  Invert = false
  LeftHanded = false
  Length = 0
  LengthCustom = 10
  MatchOuter = false
  OffsetAngle = 0
  Placement = pos=(26.7069,-184.4,35) rot=(1,0,0;1.5708rad)
  Thread = false
  Type = 36
FEATURE [Part::FeaturePython] Screw015  label="M4x10-Screw028"  # WARN: FeaturePython — macro-defined, semantics opaque (R4)
  BaseObject = -> Anti_Backlash_Nut_TR8x003 [Part__Feature030.Edge158]
  Diameter = 1
  Invert = false
  LeftHanded = false
  Length = 0
  LengthCustom = 10
  MatchOuter = false
  OffsetAngle = 0
  Placement = pos=(18.7069,-184.4,43) rot=(1,0,0;1.5708rad)
  Thread = false
  Type = 36
FEATURE [App::Part] Part010  label="Xprofile"
  Group = -> [Body018]
  Origin = -> Origin035
FEATURE [Sketcher::SketchObject] Sketch028
  ArcFitTolerance = 1e-06
  AttachmentSupport = -> [Pad004]
  ExternalGeometry = -> [Pad004]
  FullyConstrained = false
  MakeInternals = false
  MapMode = 5
  Placement = pos=(0,0,0) rot=(0,0,1;3.14159rad)
  sketch-geometry (5):
    g0: LineSegment [constr] StartX=0 StartY=200 StartZ=0 EndX=-20 EndY=200 EndZ=0
    g1: LineSegment [constr] StartX=-20 StartY=200 StartZ=0 EndX=-20 EndY=220 EndZ=0
    g2: LineSegment [constr] StartX=-20 StartY=200 StartZ=0 EndX=-20 EndY=180 EndZ=0
    g3: Circle CenterX=-20 CenterY=180 CenterZ=0 NormalX=0 NormalY=0 NormalZ=1 AngleXU=0 Radius=2
    g4: Circle CenterX=-20 CenterY=220 CenterZ=0 NormalX=0 NormalY=0 NormalZ=1 AngleXU=0 Radius=2
  constraints (12):
    c: Symmetric(g-3,g-3,g0)
    c: Horizontal(g0)
    c: Coincident(g1,g0)
    c: Vertical(g1)
    c: Coincident(g2,g0)
    c: Vertical(g2)
    c: Diameter(g3) = 4
    c: Coincident(g3,g2)
    c: Diameter(g4) = 4
    c: Coincident(g4,g1)
    c: DistanceY(g2,g2) = 20
    c: DistanceY(g1,g1) = 20
FEATURE [PartDesign::Hole] Hole
  BaseFeature = -> Pad004
  CustomThreadClearance = 0
  Depth = 25
  DepthType = 0
  Diameter = 3.3
  DrillForDepth = false
  DrillPoint = 1
  DrillPointAngle = 118
  HoleCutCountersinkAngle = 90
  HoleCutCustomValues = false
  HoleCutDepth = 0
  HoleCutDiameter = 6.1
  HoleCutType = 0
  ModelThread = false
  Placement = pos=(0,0,0) rot=(1,0,0;1.5708rad)
  Profile = -> Sketch028
  Suppressed = false
  Tapered = false
  TaperedAngle = 90
  ThreadClass = 0
  ThreadDepth = 25
  ThreadDepthType = 0
  ThreadDirection = 0
  ThreadFit = 0
  ThreadSize = 11
  ThreadType = 1
  Threaded = true
  UseCustomThreadClearance = false
FEATURE [PartDesign::Chamfer] Chamfer
  Angle = 45
  Base = -> Hole [Edge31,Edge30]
  BaseFeature = -> Hole
  ChamferType = 0
  FlipDirection = false
  Placement = pos=(0,0,0) rot=(1,0,0;1.5708rad)
  Size = 0.4
  Size2 = 1
  SupportTransform = false
  Suppressed = false
  UseAllEdges = false
FEATURE [PartDesign::Body] Body004
  AllowCompound = false
  Group = -> [Sketch004,Pad004,Sketch028,Hole,Chamfer]
  Origin = -> Origin007
  Placement = pos=(386,40,0) rot=(0,0,1;4.71239rad)
  Tip = -> Chamfer
FEATURE [App::FeaturePython] Temporary_joint  # Assembly joint (typed FeaturePython)
  Activated = true
  AngleMax = 0
  AngleMin = 0
  Detach1 = false
  Detach2 = false
  Distance = 0
  Distance2 = 0
  EnableAngleMax = false
  EnableAngleMin = false
  EnableLengthMax = false
  EnableLengthMin = false
  JointType = 0 (Fixed)
  LengthMax = 0
  LengthMin = 0
FEATURE [App::Part] Part002  label="top frame"
  Group = -> [Body001,Body002,Body004,Body013,Body014,Body015,Temporary_joint]
  Origin = -> Origin003
